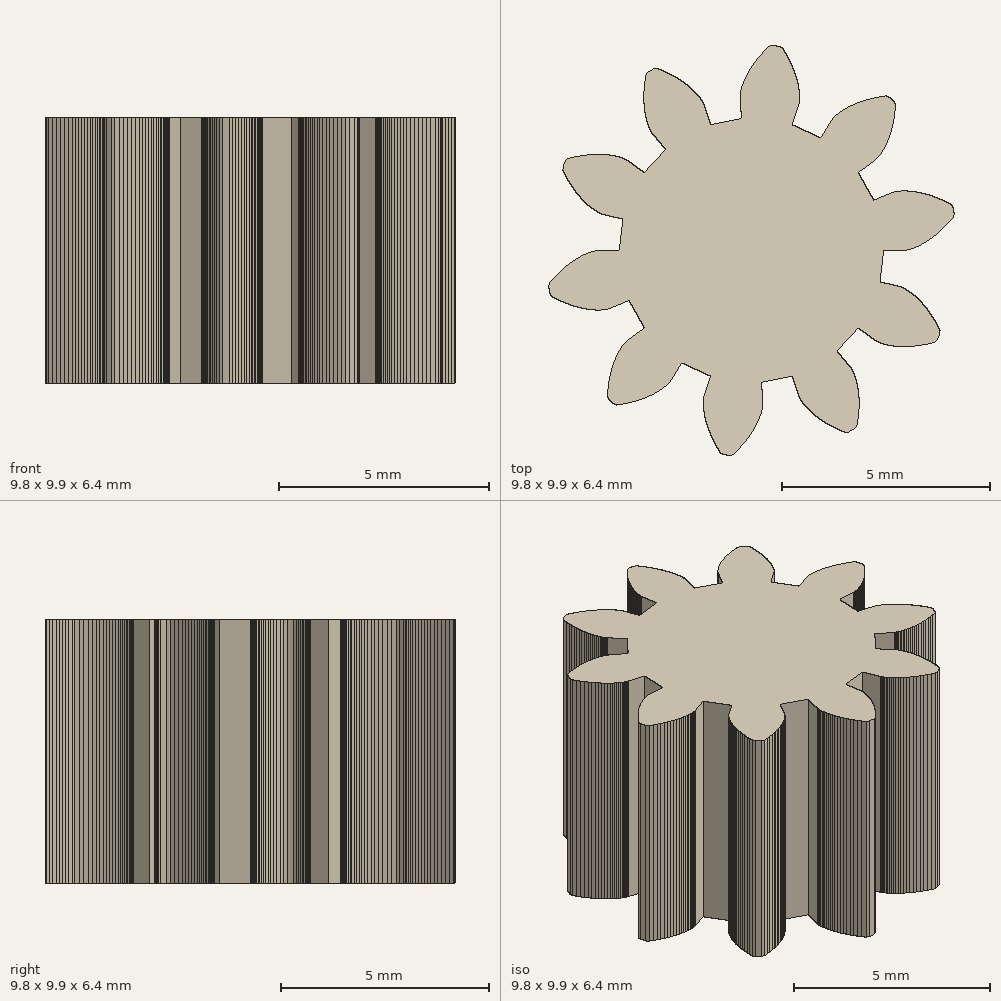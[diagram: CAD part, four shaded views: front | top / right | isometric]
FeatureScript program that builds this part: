
annotation { "Feature Type Name" : "Feature", "Feature Type Description" : "" }
export const myFeature = defineFeature(function(context is Context, id is Id, definition is map)
    precondition{}
    {
        {
            var Q0;
            Q0=qCreatedBy(makeId("Top.planeOp"),FACE);
            var sketch = newSketch(context, id + "F0", { "sketchPlane" : qUnion([Q0])});
            skLineSegment(sketch, "E0", {"start": v(1, 0) * mm, "end": v(1.16, 0) * mm});
            skLineSegment(sketch, "E1", {"start": v(1.16, 0) * mm, "end": v(1.16, 0) * mm});
            skLineSegment(sketch, "E2", {"start": v(1.16, 0) * mm, "end": v(1.17, 0) * mm});
            skLineSegment(sketch, "E3", {"start": v(1.17, 0) * mm, "end": v(1.17, 0) * mm});
            skLineSegment(sketch, "E4", {"start": v(1.17, 0) * mm, "end": v(1.18, 0) * mm});
            skLineSegment(sketch, "E5", {"start": v(1.18, 0) * mm, "end": v(1.19, 0) * mm});
            skLineSegment(sketch, "E6", {"start": v(1.19, 0) * mm, "end": v(1.2, 0) * mm});
            skLineSegment(sketch, "E7", {"start": v(1.2, 0) * mm, "end": v(1.21, 0.01) * mm});
            skLineSegment(sketch, "E8", {"start": v(1.21, 0.01) * mm, "end": v(1.22, 0.01) * mm});
            skLineSegment(sketch, "E9", {"start": v(1.22, 0.01) * mm, "end": v(1.24, 0.02) * mm});
            skLineSegment(sketch, "E10", {"start": v(1.24, 0.02) * mm, "end": v(1.25, 0.02) * mm});
            skLineSegment(sketch, "E11", {"start": v(1.25, 0.02) * mm, "end": v(1.27, 0.03) * mm});
            skLineSegment(sketch, "E12", {"start": v(1.27, 0.03) * mm, "end": v(1.28, 0.04) * mm});
            skLineSegment(sketch, "E13", {"start": v(1.28, 0.04) * mm, "end": v(1.3, 0.05) * mm});
            skLineSegment(sketch, "E14", {"start": v(1.3, 0.05) * mm, "end": v(1.32, 0.06) * mm});
            skLineSegment(sketch, "E15", {"start": v(1.32, 0.06) * mm, "end": v(1.34, 0.07) * mm});
            skLineSegment(sketch, "E16", {"start": v(1.34, 0.07) * mm, "end": v(1.36, 0.08) * mm});
            skLineSegment(sketch, "E17", {"start": v(1.36, 0.08) * mm, "end": v(1.38, 0.1) * mm});
            skLineSegment(sketch, "E18", {"start": v(1.38, 0.1) * mm, "end": v(1.4, 0.12) * mm});
            skLineSegment(sketch, "E19", {"start": v(1.4, 0.12) * mm, "end": v(1.42, 0.13) * mm});
            skLineSegment(sketch, "E20", {"start": v(1.42, 0.13) * mm, "end": v(1.44, 0.15) * mm});
            skLineSegment(sketch, "E21", {"start": v(1.44, 0.15) * mm, "end": v(1.46, 0.18) * mm});
            skLineSegment(sketch, "E22", {"start": v(1.46, 0.18) * mm, "end": v(1.49, 0.2) * mm});
            skLineSegment(sketch, "E23", {"start": v(1.49, 0.2) * mm, "end": v(1.5, 0.22) * mm});
            skLineSegment(sketch, "E24", {"start": v(1.5, 0.22) * mm, "end": v(1.53, 0.25) * mm});
            skLineSegment(sketch, "E25", {"start": v(1.53, 0.25) * mm, "end": v(1.54, 0.28) * mm});
            skLineSegment(sketch, "E26", {"start": v(1.54, 0.28) * mm, "end": v(1.53, 0.33) * mm});
            skLineSegment(sketch, "E27", {"start": v(1.53, 0.33) * mm, "end": v(1.51, 0.35) * mm});
            skLineSegment(sketch, "E28", {"start": v(1.51, 0.35) * mm, "end": v(1.48, 0.37) * mm});
            skLineSegment(sketch, "E29", {"start": v(1.48, 0.37) * mm, "end": v(1.45, 0.38) * mm});
            skLineSegment(sketch, "E30", {"start": v(1.45, 0.38) * mm, "end": v(1.42, 0.4) * mm});
            skLineSegment(sketch, "E31", {"start": v(1.42, 0.4) * mm, "end": v(1.4, 0.4) * mm});
            skLineSegment(sketch, "E32", {"start": v(1.4, 0.4) * mm, "end": v(1.37, 0.41) * mm});
            skLineSegment(sketch, "E33", {"start": v(1.37, 0.41) * mm, "end": v(1.34, 0.42) * mm});
            skLineSegment(sketch, "E34", {"start": v(1.34, 0.42) * mm, "end": v(1.31, 0.43) * mm});
            skLineSegment(sketch, "E35", {"start": v(1.31, 0.43) * mm, "end": v(1.29, 0.44) * mm});
            skLineSegment(sketch, "E36", {"start": v(1.29, 0.44) * mm, "end": v(1.26, 0.44) * mm});
            skLineSegment(sketch, "E37", {"start": v(1.26, 0.44) * mm, "end": v(1.24, 0.45) * mm});
            skLineSegment(sketch, "E38", {"start": v(1.24, 0.45) * mm, "end": v(1.22, 0.45) * mm});
            skLineSegment(sketch, "E39", {"start": v(1.22, 0.45) * mm, "end": v(1.2, 0.45) * mm});
            skLineSegment(sketch, "E40", {"start": v(1.2, 0.45) * mm, "end": v(1.18, 0.45) * mm});
            skLineSegment(sketch, "E41", {"start": v(1.18, 0.45) * mm, "end": v(1.17, 0.45) * mm});
            skLineSegment(sketch, "E42", {"start": v(1.17, 0.45) * mm, "end": v(1.15, 0.45) * mm});
            skLineSegment(sketch, "E43", {"start": v(1.15, 0.45) * mm, "end": v(1.14, 0.45) * mm});
            skLineSegment(sketch, "E44", {"start": v(1.14, 0.45) * mm, "end": v(1.12, 0.45) * mm});
            skLineSegment(sketch, "E45", {"start": v(1.12, 0.45) * mm, "end": v(1.11, 0.45) * mm});
            skLineSegment(sketch, "E46", {"start": v(1.11, 0.45) * mm, "end": v(1.1, 0.45) * mm});
            skLineSegment(sketch, "E47", {"start": v(1.1, 0.45) * mm, "end": v(1.1, 0.45) * mm});
            skLineSegment(sketch, "E48", {"start": v(1.1, 0.45) * mm, "end": v(1.09, 0.44) * mm});
            skLineSegment(sketch, "E49", {"start": v(1.09, 0.44) * mm, "end": v(1.08, 0.44) * mm});
            skLineSegment(sketch, "E50", {"start": v(1.08, 0.44) * mm, "end": v(1.08, 0.44) * mm});
            skLineSegment(sketch, "E51", {"start": v(1.08, 0.44) * mm, "end": v(1.07, 0.44) * mm});
            skLineSegment(sketch, "E52", {"start": v(1.07, 0.44) * mm, "end": v(1.07, 0.44) * mm});
            skLineSegment(sketch, "E53", {"start": v(1.07, 0.44) * mm, "end": v(0.93, 0.38) * mm});
            skLineSegment(sketch, "E54", {"start": v(0.93, 0.38) * mm, "end": v(0.81, 0.59) * mm});
            skLineSegment(sketch, "E55", {"start": v(0.81, 0.59) * mm, "end": v(0.94, 0.68) * mm});
            skLineSegment(sketch, "E56", {"start": v(0.94, 0.68) * mm, "end": v(0.94, 0.68) * mm});
            skLineSegment(sketch, "E57", {"start": v(0.94, 0.68) * mm, "end": v(0.95, 0.69) * mm});
            skLineSegment(sketch, "E58", {"start": v(0.95, 0.69) * mm, "end": v(0.95, 0.7) * mm});
            skLineSegment(sketch, "E59", {"start": v(0.95, 0.7) * mm, "end": v(0.95, 0.7) * mm});
            skLineSegment(sketch, "E60", {"start": v(0.95, 0.7) * mm, "end": v(0.96, 0.7) * mm});
            skLineSegment(sketch, "E61", {"start": v(0.96, 0.7) * mm, "end": v(0.97, 0.71) * mm});
            skLineSegment(sketch, "E62", {"start": v(0.97, 0.71) * mm, "end": v(0.97, 0.72) * mm});
            skLineSegment(sketch, "E63", {"start": v(0.97, 0.72) * mm, "end": v(0.98, 0.73) * mm});
            skLineSegment(sketch, "E64", {"start": v(0.98, 0.73) * mm, "end": v(0.99, 0.74) * mm});
            skLineSegment(sketch, "E65", {"start": v(0.99, 0.74) * mm, "end": v(1, 0.75) * mm});
            skLineSegment(sketch, "E66", {"start": v(1, 0.75) * mm, "end": v(1, 0.77) * mm});
            skLineSegment(sketch, "E67", {"start": v(1, 0.77) * mm, "end": v(1.01, 0.79) * mm});
            skLineSegment(sketch, "E68", {"start": v(1.01, 0.79) * mm, "end": v(1.02, 0.8) * mm});
            skLineSegment(sketch, "E69", {"start": v(1.02, 0.8) * mm, "end": v(1.03, 0.82) * mm});
            skLineSegment(sketch, "E70", {"start": v(1.03, 0.82) * mm, "end": v(1.04, 0.84) * mm});
            skLineSegment(sketch, "E71", {"start": v(1.04, 0.84) * mm, "end": v(1.05, 0.87) * mm});
            skLineSegment(sketch, "E72", {"start": v(1.05, 0.87) * mm, "end": v(1.06, 0.9) * mm});
            skLineSegment(sketch, "E73", {"start": v(1.06, 0.9) * mm, "end": v(1.06, 0.92) * mm});
            skLineSegment(sketch, "E74", {"start": v(1.06, 0.92) * mm, "end": v(1.07, 0.94) * mm});
            skLineSegment(sketch, "E75", {"start": v(1.07, 0.94) * mm, "end": v(1.08, 0.97) * mm});
            skLineSegment(sketch, "E76", {"start": v(1.08, 0.97) * mm, "end": v(1.08, 1) * mm});
            skLineSegment(sketch, "E77", {"start": v(1.08, 1) * mm, "end": v(1.09, 1.04) * mm});
            skLineSegment(sketch, "E78", {"start": v(1.09, 1.04) * mm, "end": v(1.09, 1.07) * mm});
            skLineSegment(sketch, "E79", {"start": v(1.09, 1.07) * mm, "end": v(1.1, 1.1) * mm});
            skLineSegment(sketch, "E80", {"start": v(1.1, 1.1) * mm, "end": v(1.08, 1.13) * mm});
            skLineSegment(sketch, "E81", {"start": v(1.08, 1.13) * mm, "end": v(1.04, 1.16) * mm});
            skLineSegment(sketch, "E82", {"start": v(1.04, 1.16) * mm, "end": v(1.02, 1.17) * mm});
            skLineSegment(sketch, "E83", {"start": v(1.02, 1.17) * mm, "end": v(0.98, 1.17) * mm});
            skLineSegment(sketch, "E84", {"start": v(0.98, 1.17) * mm, "end": v(0.95, 1.16) * mm});
            skLineSegment(sketch, "E85", {"start": v(0.95, 1.16) * mm, "end": v(0.92, 1.15) * mm});
            skLineSegment(sketch, "E86", {"start": v(0.92, 1.15) * mm, "end": v(0.89, 1.15) * mm});
            skLineSegment(sketch, "E87", {"start": v(0.89, 1.15) * mm, "end": v(0.86, 1.14) * mm});
            skLineSegment(sketch, "E88", {"start": v(0.86, 1.14) * mm, "end": v(0.83, 1.13) * mm});
            skLineSegment(sketch, "E89", {"start": v(0.83, 1.13) * mm, "end": v(0.8, 1.12) * mm});
            skLineSegment(sketch, "E90", {"start": v(0.8, 1.12) * mm, "end": v(0.79, 1.1) * mm});
            skLineSegment(sketch, "E91", {"start": v(0.79, 1.1) * mm, "end": v(0.76, 1.1) * mm});
            skLineSegment(sketch, "E92", {"start": v(0.76, 1.1) * mm, "end": v(0.74, 1.1) * mm});
            skLineSegment(sketch, "E93", {"start": v(0.74, 1.1) * mm, "end": v(0.72, 1.08) * mm});
            skLineSegment(sketch, "E94", {"start": v(0.72, 1.08) * mm, "end": v(0.7, 1.07) * mm});
            skLineSegment(sketch, "E95", {"start": v(0.7, 1.07) * mm, "end": v(0.7, 1.06) * mm});
            skLineSegment(sketch, "E96", {"start": v(0.7, 1.06) * mm, "end": v(0.68, 1.05) * mm});
            skLineSegment(sketch, "E97", {"start": v(0.68, 1.05) * mm, "end": v(0.67, 1.04) * mm});
            skLineSegment(sketch, "E98", {"start": v(0.67, 1.04) * mm, "end": v(0.65, 1.03) * mm});
            skLineSegment(sketch, "E99", {"start": v(0.65, 1.03) * mm, "end": v(0.64, 1.02) * mm});
            skLineSegment(sketch, "E100", {"start": v(0.64, 1.02) * mm, "end": v(0.64, 1.02) * mm});
            skLineSegment(sketch, "E101", {"start": v(0.64, 1.02) * mm, "end": v(0.63, 1) * mm});
            skLineSegment(sketch, "E102", {"start": v(0.63, 1) * mm, "end": v(0.62, 1) * mm});
            skLineSegment(sketch, "E103", {"start": v(0.62, 1) * mm, "end": v(0.62, 1) * mm});
            skLineSegment(sketch, "E104", {"start": v(0.62, 1) * mm, "end": v(0.61, 1) * mm});
            skLineSegment(sketch, "E105", {"start": v(0.61, 1) * mm, "end": v(0.61, 1) * mm});
            skLineSegment(sketch, "E106", {"start": v(0.61, 1) * mm, "end": v(0.61, 0.99) * mm});
            skLineSegment(sketch, "E107", {"start": v(0.61, 0.99) * mm, "end": v(0.6, 0.99) * mm});
            skLineSegment(sketch, "E108", {"start": v(0.6, 0.99) * mm, "end": v(0.53, 0.85) * mm});
            skLineSegment(sketch, "E109", {"start": v(0.53, 0.85) * mm, "end": v(0.3, 0.95) * mm});
            skLineSegment(sketch, "E110", {"start": v(0.3, 0.95) * mm, "end": v(0.36, 1.1) * mm});
            skLineSegment(sketch, "E111", {"start": v(0.36, 1.1) * mm, "end": v(0.36, 1.1) * mm});
            skLineSegment(sketch, "E112", {"start": v(0.36, 1.1) * mm, "end": v(0.36, 1.11) * mm});
            skLineSegment(sketch, "E113", {"start": v(0.36, 1.11) * mm, "end": v(0.36, 1.12) * mm});
            skLineSegment(sketch, "E114", {"start": v(0.36, 1.12) * mm, "end": v(0.36, 1.12) * mm});
            skLineSegment(sketch, "E115", {"start": v(0.36, 1.12) * mm, "end": v(0.36, 1.13) * mm});
            skLineSegment(sketch, "E116", {"start": v(0.36, 1.13) * mm, "end": v(0.36, 1.14) * mm});
            skLineSegment(sketch, "E117", {"start": v(0.36, 1.14) * mm, "end": v(0.36, 1.15) * mm});
            skLineSegment(sketch, "E118", {"start": v(0.36, 1.15) * mm, "end": v(0.36, 1.17) * mm});
            skLineSegment(sketch, "E119", {"start": v(0.36, 1.17) * mm, "end": v(0.36, 1.18) * mm});
            skLineSegment(sketch, "E120", {"start": v(0.36, 1.18) * mm, "end": v(0.36, 1.2) * mm});
            skLineSegment(sketch, "E121", {"start": v(0.36, 1.2) * mm, "end": v(0.36, 1.21) * mm});
            skLineSegment(sketch, "E122", {"start": v(0.36, 1.21) * mm, "end": v(0.36, 1.23) * mm});
            skLineSegment(sketch, "E123", {"start": v(0.36, 1.23) * mm, "end": v(0.36, 1.25) * mm});
            skLineSegment(sketch, "E124", {"start": v(0.36, 1.25) * mm, "end": v(0.35, 1.27) * mm});
            skLineSegment(sketch, "E125", {"start": v(0.35, 1.27) * mm, "end": v(0.35, 1.3) * mm});
            skLineSegment(sketch, "E126", {"start": v(0.35, 1.3) * mm, "end": v(0.34, 1.32) * mm});
            skLineSegment(sketch, "E127", {"start": v(0.34, 1.32) * mm, "end": v(0.33, 1.34) * mm});
            skLineSegment(sketch, "E128", {"start": v(0.33, 1.34) * mm, "end": v(0.32, 1.37) * mm});
            skLineSegment(sketch, "E129", {"start": v(0.32, 1.37) * mm, "end": v(0.31, 1.4) * mm});
            skLineSegment(sketch, "E130", {"start": v(0.31, 1.4) * mm, "end": v(0.3, 1.42) * mm});
            skLineSegment(sketch, "E131", {"start": v(0.3, 1.42) * mm, "end": v(0.29, 1.45) * mm});
            skLineSegment(sketch, "E132", {"start": v(0.29, 1.45) * mm, "end": v(0.27, 1.48) * mm});
            skLineSegment(sketch, "E133", {"start": v(0.27, 1.48) * mm, "end": v(0.25, 1.5) * mm});
            skLineSegment(sketch, "E134", {"start": v(0.25, 1.5) * mm, "end": v(0.23, 1.54) * mm});
            skLineSegment(sketch, "E135", {"start": v(0.23, 1.54) * mm, "end": v(0.21, 1.55) * mm});
            skLineSegment(sketch, "E136", {"start": v(0.21, 1.55) * mm, "end": v(0.16, 1.55) * mm});
            skLineSegment(sketch, "E137", {"start": v(0.16, 1.55) * mm, "end": v(0.14, 1.55) * mm});
            skLineSegment(sketch, "E138", {"start": v(0.14, 1.55) * mm, "end": v(0.11, 1.52) * mm});
            skLineSegment(sketch, "E139", {"start": v(0.11, 1.52) * mm, "end": v(0.09, 1.5) * mm});
            skLineSegment(sketch, "E140", {"start": v(0.09, 1.5) * mm, "end": v(0.07, 1.47) * mm});
            skLineSegment(sketch, "E141", {"start": v(0.07, 1.47) * mm, "end": v(0.05, 1.45) * mm});
            skLineSegment(sketch, "E142", {"start": v(0.05, 1.45) * mm, "end": v(0.03, 1.43) * mm});
            skLineSegment(sketch, "E143", {"start": v(0.03, 1.43) * mm, "end": v(0.01, 1.4) * mm});
            skLineSegment(sketch, "E144", {"start": v(0.01, 1.4) * mm, "end": v(0, 1.38) * mm});
            skLineSegment(sketch, "E145", {"start": v(0, 1.38) * mm, "end": v(-0.02, 1.36) * mm});
            skLineSegment(sketch, "E146", {"start": v(-0.02, 1.36) * mm, "end": v(-0.03, 1.34) * mm});
            skLineSegment(sketch, "E147", {"start": v(-0.03, 1.34) * mm, "end": v(-0.04, 1.32) * mm});
            skLineSegment(sketch, "E148", {"start": v(-0.04, 1.32) * mm, "end": v(-0.05, 1.3) * mm});
            skLineSegment(sketch, "E149", {"start": v(-0.05, 1.3) * mm, "end": v(-0.06, 1.28) * mm});
            skLineSegment(sketch, "E150", {"start": v(-0.06, 1.28) * mm, "end": v(-0.06, 1.26) * mm});
            skLineSegment(sketch, "E151", {"start": v(-0.06, 1.26) * mm, "end": v(-0.07, 1.25) * mm});
            skLineSegment(sketch, "E152", {"start": v(-0.07, 1.25) * mm, "end": v(-0.07, 1.23) * mm});
            skLineSegment(sketch, "E153", {"start": v(-0.07, 1.23) * mm, "end": v(-0.08, 1.22) * mm});
            skLineSegment(sketch, "E154", {"start": v(-0.08, 1.22) * mm, "end": v(-0.08, 1.2) * mm});
            skLineSegment(sketch, "E155", {"start": v(-0.08, 1.2) * mm, "end": v(-0.08, 1.2) * mm});
            skLineSegment(sketch, "E156", {"start": v(-0.08, 1.2) * mm, "end": v(-0.08, 1.19) * mm});
            skLineSegment(sketch, "E157", {"start": v(-0.08, 1.19) * mm, "end": v(-0.09, 1.18) * mm});
            skLineSegment(sketch, "E158", {"start": v(-0.09, 1.18) * mm, "end": v(-0.09, 1.17) * mm});
            skLineSegment(sketch, "E159", {"start": v(-0.09, 1.17) * mm, "end": v(-0.09, 1.17) * mm});
            skLineSegment(sketch, "E160", {"start": v(-0.09, 1.17) * mm, "end": v(-0.09, 1.16) * mm});
            skLineSegment(sketch, "E161", {"start": v(-0.09, 1.16) * mm, "end": v(-0.09, 1.16) * mm});
            skLineSegment(sketch, "E162", {"start": v(-0.09, 1.16) * mm, "end": v(-0.08, 1) * mm});
            skLineSegment(sketch, "E163", {"start": v(-0.08, 1) * mm, "end": v(-0.3, 0.95) * mm});
            skLineSegment(sketch, "E164", {"start": v(-0.3, 0.95) * mm, "end": v(-0.36, 1.1) * mm});
            skLineSegment(sketch, "E165", {"start": v(-0.36, 1.1) * mm, "end": v(-0.36, 1.1) * mm});
            skLineSegment(sketch, "E166", {"start": v(-0.36, 1.1) * mm, "end": v(-0.36, 1.11) * mm});
            skLineSegment(sketch, "E167", {"start": v(-0.36, 1.11) * mm, "end": v(-0.36, 1.12) * mm});
            skLineSegment(sketch, "E168", {"start": v(-0.36, 1.12) * mm, "end": v(-0.37, 1.12) * mm});
            skLineSegment(sketch, "E169", {"start": v(-0.37, 1.12) * mm, "end": v(-0.37, 1.13) * mm});
            skLineSegment(sketch, "E170", {"start": v(-0.37, 1.13) * mm, "end": v(-0.38, 1.14) * mm});
            skLineSegment(sketch, "E171", {"start": v(-0.38, 1.14) * mm, "end": v(-0.38, 1.15) * mm});
            skLineSegment(sketch, "E172", {"start": v(-0.38, 1.15) * mm, "end": v(-0.4, 1.16) * mm});
            skLineSegment(sketch, "E173", {"start": v(-0.4, 1.16) * mm, "end": v(-0.4, 1.17) * mm});
            skLineSegment(sketch, "E174", {"start": v(-0.4, 1.17) * mm, "end": v(-0.4, 1.18) * mm});
            skLineSegment(sketch, "E175", {"start": v(-0.4, 1.18) * mm, "end": v(-0.42, 1.2) * mm});
            skLineSegment(sketch, "E176", {"start": v(-0.42, 1.2) * mm, "end": v(-0.43, 1.2) * mm});
            skLineSegment(sketch, "E177", {"start": v(-0.43, 1.2) * mm, "end": v(-0.45, 1.22) * mm});
            skLineSegment(sketch, "E178", {"start": v(-0.45, 1.22) * mm, "end": v(-0.46, 1.23) * mm});
            skLineSegment(sketch, "E179", {"start": v(-0.46, 1.23) * mm, "end": v(-0.48, 1.25) * mm});
            skLineSegment(sketch, "E180", {"start": v(-0.48, 1.25) * mm, "end": v(-0.5, 1.26) * mm});
            skLineSegment(sketch, "E181", {"start": v(-0.5, 1.26) * mm, "end": v(-0.52, 1.28) * mm});
            skLineSegment(sketch, "E182", {"start": v(-0.52, 1.28) * mm, "end": v(-0.54, 1.3) * mm});
            skLineSegment(sketch, "E183", {"start": v(-0.54, 1.3) * mm, "end": v(-0.57, 1.3) * mm});
            skLineSegment(sketch, "E184", {"start": v(-0.57, 1.3) * mm, "end": v(-0.6, 1.32) * mm});
            skLineSegment(sketch, "E185", {"start": v(-0.6, 1.32) * mm, "end": v(-0.62, 1.34) * mm});
            skLineSegment(sketch, "E186", {"start": v(-0.62, 1.34) * mm, "end": v(-0.65, 1.35) * mm});
            skLineSegment(sketch, "E187", {"start": v(-0.65, 1.35) * mm, "end": v(-0.68, 1.37) * mm});
            skLineSegment(sketch, "E188", {"start": v(-0.68, 1.37) * mm, "end": v(-0.71, 1.38) * mm});
            skLineSegment(sketch, "E189", {"start": v(-0.71, 1.38) * mm, "end": v(-0.74, 1.38) * mm});
            skLineSegment(sketch, "E190", {"start": v(-0.74, 1.38) * mm, "end": v(-0.79, 1.36) * mm});
            skLineSegment(sketch, "E191", {"start": v(-0.78, 1.35) * mm, "end": v(-0.8, 1.33) * mm});
            skLineSegment(sketch, "E192", {"start": v(-0.8, 1.33) * mm, "end": v(-0.8, 1.3) * mm});
            skLineSegment(sketch, "E193", {"start": v(-0.8, 1.3) * mm, "end": v(-0.81, 1.26) * mm});
            skLineSegment(sketch, "E194", {"start": v(-0.81, 1.26) * mm, "end": v(-0.81, 1.23) * mm});
            skLineSegment(sketch, "E195", {"start": v(-0.81, 1.23) * mm, "end": v(-0.82, 1.2) * mm});
            skLineSegment(sketch, "E196", {"start": v(-0.82, 1.2) * mm, "end": v(-0.82, 1.17) * mm});
            skLineSegment(sketch, "E197", {"start": v(-0.82, 1.17) * mm, "end": v(-0.82, 1.14) * mm});
            skLineSegment(sketch, "E198", {"start": v(-0.82, 1.14) * mm, "end": v(-0.81, 1.12) * mm});
            skLineSegment(sketch, "E199", {"start": v(-0.81, 1.12) * mm, "end": v(-0.81, 1.09) * mm});
            skLineSegment(sketch, "E200", {"start": v(-0.81, 1.09) * mm, "end": v(-0.81, 1.07) * mm});
            skLineSegment(sketch, "E201", {"start": v(-0.81, 1.07) * mm, "end": v(-0.8, 1.04) * mm});
            skLineSegment(sketch, "E202", {"start": v(-0.8, 1.04) * mm, "end": v(-0.8, 1.02) * mm});
            skLineSegment(sketch, "E203", {"start": v(-0.8, 1.02) * mm, "end": v(-0.8, 1) * mm});
            skLineSegment(sketch, "E204", {"start": v(-0.8, 1) * mm, "end": v(-0.8, 0.99) * mm});
            skLineSegment(sketch, "E205", {"start": v(-0.8, 0.99) * mm, "end": v(-0.79, 0.97) * mm});
            skLineSegment(sketch, "E206", {"start": v(-0.79, 0.97) * mm, "end": v(-0.78, 0.95) * mm});
            skLineSegment(sketch, "E207", {"start": v(-0.78, 0.95) * mm, "end": v(-0.78, 0.94) * mm});
            skLineSegment(sketch, "E208", {"start": v(-0.78, 0.94) * mm, "end": v(-0.78, 0.93) * mm});
            skLineSegment(sketch, "E209", {"start": v(-0.78, 0.93) * mm, "end": v(-0.77, 0.92) * mm});
            skLineSegment(sketch, "E210", {"start": v(-0.77, 0.92) * mm, "end": v(-0.77, 0.91) * mm});
            skLineSegment(sketch, "E211", {"start": v(-0.77, 0.91) * mm, "end": v(-0.76, 0.9) * mm});
            skLineSegment(sketch, "E212", {"start": v(-0.76, 0.9) * mm, "end": v(-0.76, 0.9) * mm});
            skLineSegment(sketch, "E213", {"start": v(-0.76, 0.9) * mm, "end": v(-0.75, 0.89) * mm});
            skLineSegment(sketch, "E214", {"start": v(-0.75, 0.89) * mm, "end": v(-0.75, 0.89) * mm});
            skLineSegment(sketch, "E215", {"start": v(-0.75, 0.89) * mm, "end": v(-0.75, 0.88) * mm});
            skLineSegment(sketch, "E216", {"start": v(-0.75, 0.88) * mm, "end": v(-0.65, 0.76) * mm});
            skLineSegment(sketch, "E217", {"start": v(-0.65, 0.76) * mm, "end": v(-0.81, 0.59) * mm});
            skLineSegment(sketch, "E218", {"start": v(-0.81, 0.59) * mm, "end": v(-0.94, 0.68) * mm});
            skLineSegment(sketch, "E219", {"start": v(-0.94, 0.68) * mm, "end": v(-0.94, 0.68) * mm});
            skLineSegment(sketch, "E220", {"start": v(-0.94, 0.68) * mm, "end": v(-0.95, 0.69) * mm});
            skLineSegment(sketch, "E221", {"start": v(-0.95, 0.69) * mm, "end": v(-0.95, 0.69) * mm});
            skLineSegment(sketch, "E222", {"start": v(-0.95, 0.69) * mm, "end": v(-0.96, 0.7) * mm});
            skLineSegment(sketch, "E223", {"start": v(-0.96, 0.7) * mm, "end": v(-0.97, 0.7) * mm});
            skLineSegment(sketch, "E224", {"start": v(-0.97, 0.7) * mm, "end": v(-0.97, 0.7) * mm});
            skLineSegment(sketch, "E225", {"start": v(-0.97, 0.7) * mm, "end": v(-0.98, 0.7) * mm});
            skLineSegment(sketch, "E226", {"start": v(-0.98, 0.7) * mm, "end": v(-1, 0.7) * mm});
            skLineSegment(sketch, "E227", {"start": v(-1, 0.7) * mm, "end": v(-1.01, 0.71) * mm});
            skLineSegment(sketch, "E228", {"start": v(-1.01, 0.71) * mm, "end": v(-1.03, 0.71) * mm});
            skLineSegment(sketch, "E229", {"start": v(-1.03, 0.71) * mm, "end": v(-1.04, 0.72) * mm});
            skLineSegment(sketch, "E230", {"start": v(-1.04, 0.72) * mm, "end": v(-1.06, 0.72) * mm});
            skLineSegment(sketch, "E231", {"start": v(-1.06, 0.72) * mm, "end": v(-1.08, 0.72) * mm});
            skLineSegment(sketch, "E232", {"start": v(-1.08, 0.72) * mm, "end": v(-1.1, 0.73) * mm});
            skLineSegment(sketch, "E233", {"start": v(-1.1, 0.73) * mm, "end": v(-1.12, 0.73) * mm});
            skLineSegment(sketch, "E234", {"start": v(-1.12, 0.73) * mm, "end": v(-1.15, 0.73) * mm});
            skLineSegment(sketch, "E235", {"start": v(-1.15, 0.73) * mm, "end": v(-1.17, 0.73) * mm});
            skLineSegment(sketch, "E236", {"start": v(-1.17, 0.73) * mm, "end": v(-1.2, 0.73) * mm});
            skLineSegment(sketch, "E237", {"start": v(-1.2, 0.73) * mm, "end": v(-1.23, 0.73) * mm});
            skLineSegment(sketch, "E238", {"start": v(-1.23, 0.73) * mm, "end": v(-1.26, 0.72) * mm});
            skLineSegment(sketch, "E239", {"start": v(-1.26, 0.72) * mm, "end": v(-1.29, 0.72) * mm});
            skLineSegment(sketch, "E240", {"start": v(-1.29, 0.72) * mm, "end": v(-1.32, 0.71) * mm});
            skLineSegment(sketch, "E241", {"start": v(-1.32, 0.71) * mm, "end": v(-1.35, 0.7) * mm});
            skLineSegment(sketch, "E242", {"start": v(-1.35, 0.7) * mm, "end": v(-1.39, 0.7) * mm});
            skLineSegment(sketch, "E243", {"start": v(-1.39, 0.7) * mm, "end": v(-1.4, 0.68) * mm});
            skLineSegment(sketch, "E244", {"start": v(-1.4, 0.68) * mm, "end": v(-1.43, 0.63) * mm});
            skLineSegment(sketch, "E245", {"start": v(-1.43, 0.63) * mm, "end": v(-1.43, 0.6) * mm});
            skLineSegment(sketch, "E246", {"start": v(-1.43, 0.6) * mm, "end": v(-1.41, 0.58) * mm});
            skLineSegment(sketch, "E247", {"start": v(-1.41, 0.58) * mm, "end": v(-1.4, 0.55) * mm});
            skLineSegment(sketch, "E248", {"start": v(-1.4, 0.55) * mm, "end": v(-1.38, 0.52) * mm});
            skLineSegment(sketch, "E249", {"start": v(-1.38, 0.52) * mm, "end": v(-1.36, 0.5) * mm});
            skLineSegment(sketch, "E250", {"start": v(-1.36, 0.5) * mm, "end": v(-1.35, 0.47) * mm});
            skLineSegment(sketch, "E251", {"start": v(-1.35, 0.47) * mm, "end": v(-1.33, 0.44) * mm});
            skLineSegment(sketch, "E252", {"start": v(-1.33, 0.44) * mm, "end": v(-1.31, 0.42) * mm});
            skLineSegment(sketch, "E253", {"start": v(-1.31, 0.42) * mm, "end": v(-1.3, 0.4) * mm});
            skLineSegment(sketch, "E254", {"start": v(-1.3, 0.4) * mm, "end": v(-1.28, 0.39) * mm});
            skLineSegment(sketch, "E255", {"start": v(-1.28, 0.39) * mm, "end": v(-1.27, 0.37) * mm});
            skLineSegment(sketch, "E256", {"start": v(-1.27, 0.37) * mm, "end": v(-1.25, 0.36) * mm});
            skLineSegment(sketch, "E257", {"start": v(-1.25, 0.36) * mm, "end": v(-1.24, 0.34) * mm});
            skLineSegment(sketch, "E258", {"start": v(-1.24, 0.34) * mm, "end": v(-1.22, 0.33) * mm});
            skLineSegment(sketch, "E259", {"start": v(-1.22, 0.33) * mm, "end": v(-1.2, 0.32) * mm});
            skLineSegment(sketch, "E260", {"start": v(-1.2, 0.32) * mm, "end": v(-1.2, 0.31) * mm});
            skLineSegment(sketch, "E261", {"start": v(-1.2, 0.31) * mm, "end": v(-1.18, 0.3) * mm});
            skLineSegment(sketch, "E262", {"start": v(-1.18, 0.3) * mm, "end": v(-1.17, 0.3) * mm});
            skLineSegment(sketch, "E263", {"start": v(-1.17, 0.3) * mm, "end": v(-1.16, 0.3) * mm});
            skLineSegment(sketch, "E264", {"start": v(-1.16, 0.3) * mm, "end": v(-1.15, 0.29) * mm});
            skLineSegment(sketch, "E265", {"start": v(-1.15, 0.29) * mm, "end": v(-1.15, 0.28) * mm});
            skLineSegment(sketch, "E266", {"start": v(-1.15, 0.28) * mm, "end": v(-1.14, 0.28) * mm});
            skLineSegment(sketch, "E267", {"start": v(-1.14, 0.28) * mm, "end": v(-1.14, 0.28) * mm});
            skLineSegment(sketch, "E268", {"start": v(-1.14, 0.28) * mm, "end": v(-1.13, 0.28) * mm});
            skLineSegment(sketch, "E269", {"start": v(-1.13, 0.28) * mm, "end": v(-1.13, 0.28) * mm});
            skLineSegment(sketch, "E270", {"start": v(-1.13, 0.28) * mm, "end": v(-1.13, 0.27) * mm});
            skLineSegment(sketch, "E271", {"start": v(-1.13, 0.27) * mm, "end": v(-0.97, 0.24) * mm});
            skLineSegment(sketch, "E272", {"start": v(-0.97, 0.24) * mm, "end": v(-1, 0) * mm});
            skLineSegment(sketch, "E273", {"start": v(-1, 0) * mm, "end": v(-1.16, 0) * mm});
            skLineSegment(sketch, "E274", {"start": v(-1.16, 0) * mm, "end": v(-1.16, 0) * mm});
            skLineSegment(sketch, "E275", {"start": v(-1.16, 0) * mm, "end": v(-1.17, 0) * mm});
            skLineSegment(sketch, "E276", {"start": v(-1.17, 0) * mm, "end": v(-1.17, 0) * mm});
            skLineSegment(sketch, "E277", {"start": v(-1.17, 0) * mm, "end": v(-1.18, 0) * mm});
            skLineSegment(sketch, "E278", {"start": v(-1.18, 0) * mm, "end": v(-1.19, 0) * mm});
            skLineSegment(sketch, "E279", {"start": v(-1.19, 0) * mm, "end": v(-1.2, 0) * mm});
            skLineSegment(sketch, "E280", {"start": v(-1.2, 0) * mm, "end": v(-1.21, -0.01) * mm});
            skLineSegment(sketch, "E281", {"start": v(-1.21, -0.01) * mm, "end": v(-1.22, -0.01) * mm});
            skLineSegment(sketch, "E282", {"start": v(-1.22, -0.01) * mm, "end": v(-1.24, -0.02) * mm});
            skLineSegment(sketch, "E283", {"start": v(-1.24, -0.02) * mm, "end": v(-1.25, -0.02) * mm});
            skLineSegment(sketch, "E284", {"start": v(-1.25, -0.02) * mm, "end": v(-1.27, -0.03) * mm});
            skLineSegment(sketch, "E285", {"start": v(-1.27, -0.03) * mm, "end": v(-1.28, -0.04) * mm});
            skLineSegment(sketch, "E286", {"start": v(-1.28, -0.04) * mm, "end": v(-1.3, -0.05) * mm});
            skLineSegment(sketch, "E287", {"start": v(-1.3, -0.05) * mm, "end": v(-1.32, -0.06) * mm});
            skLineSegment(sketch, "E288", {"start": v(-1.32, -0.06) * mm, "end": v(-1.34, -0.07) * mm});
            skLineSegment(sketch, "E289", {"start": v(-1.34, -0.07) * mm, "end": v(-1.36, -0.08) * mm});
            skLineSegment(sketch, "E290", {"start": v(-1.36, -0.08) * mm, "end": v(-1.38, -0.1) * mm});
            skLineSegment(sketch, "E291", {"start": v(-1.38, -0.1) * mm, "end": v(-1.4, -0.12) * mm});
            skLineSegment(sketch, "E292", {"start": v(-1.4, -0.12) * mm, "end": v(-1.42, -0.13) * mm});
            skLineSegment(sketch, "E293", {"start": v(-1.42, -0.13) * mm, "end": v(-1.44, -0.15) * mm});
            skLineSegment(sketch, "E294", {"start": v(-1.44, -0.15) * mm, "end": v(-1.46, -0.18) * mm});
            skLineSegment(sketch, "E295", {"start": v(-1.46, -0.18) * mm, "end": v(-1.49, -0.2) * mm});
            skLineSegment(sketch, "E296", {"start": v(-1.49, -0.2) * mm, "end": v(-1.5, -0.22) * mm});
            skLineSegment(sketch, "E297", {"start": v(-1.5, -0.22) * mm, "end": v(-1.53, -0.25) * mm});
            skLineSegment(sketch, "E298", {"start": v(-1.53, -0.25) * mm, "end": v(-1.54, -0.28) * mm});
            skLineSegment(sketch, "E299", {"start": v(-1.54, -0.28) * mm, "end": v(-1.53, -0.33) * mm});
            skLineSegment(sketch, "E300", {"start": v(-1.53, -0.33) * mm, "end": v(-1.51, -0.35) * mm});
            skLineSegment(sketch, "E301", {"start": v(-1.51, -0.35) * mm, "end": v(-1.48, -0.37) * mm});
            skLineSegment(sketch, "E302", {"start": v(-1.48, -0.37) * mm, "end": v(-1.45, -0.38) * mm});
            skLineSegment(sketch, "E303", {"start": v(-1.45, -0.38) * mm, "end": v(-1.42, -0.4) * mm});
            skLineSegment(sketch, "E304", {"start": v(-1.42, -0.4) * mm, "end": v(-1.4, -0.4) * mm});
            skLineSegment(sketch, "E305", {"start": v(-1.4, -0.4) * mm, "end": v(-1.37, -0.41) * mm});
            skLineSegment(sketch, "E306", {"start": v(-1.37, -0.41) * mm, "end": v(-1.34, -0.42) * mm});
            skLineSegment(sketch, "E307", {"start": v(-1.34, -0.42) * mm, "end": v(-1.31, -0.43) * mm});
            skLineSegment(sketch, "E308", {"start": v(-1.31, -0.43) * mm, "end": v(-1.29, -0.44) * mm});
            skLineSegment(sketch, "E309", {"start": v(-1.29, -0.44) * mm, "end": v(-1.26, -0.44) * mm});
            skLineSegment(sketch, "E310", {"start": v(-1.26, -0.44) * mm, "end": v(-1.24, -0.45) * mm});
            skLineSegment(sketch, "E311", {"start": v(-1.24, -0.45) * mm, "end": v(-1.22, -0.45) * mm});
            skLineSegment(sketch, "E312", {"start": v(-1.22, -0.45) * mm, "end": v(-1.2, -0.45) * mm});
            skLineSegment(sketch, "E313", {"start": v(-1.2, -0.45) * mm, "end": v(-1.18, -0.45) * mm});
            skLineSegment(sketch, "E314", {"start": v(-1.18, -0.45) * mm, "end": v(-1.17, -0.45) * mm});
            skLineSegment(sketch, "E315", {"start": v(-1.17, -0.45) * mm, "end": v(-1.15, -0.45) * mm});
            skLineSegment(sketch, "E316", {"start": v(-1.15, -0.45) * mm, "end": v(-1.14, -0.45) * mm});
            skLineSegment(sketch, "E317", {"start": v(-1.14, -0.45) * mm, "end": v(-1.12, -0.45) * mm});
            skLineSegment(sketch, "E318", {"start": v(-1.12, -0.45) * mm, "end": v(-1.11, -0.45) * mm});
            skLineSegment(sketch, "E319", {"start": v(-1.11, -0.45) * mm, "end": v(-1.1, -0.45) * mm});
            skLineSegment(sketch, "E320", {"start": v(-1.1, -0.45) * mm, "end": v(-1.1, -0.45) * mm});
            skLineSegment(sketch, "E321", {"start": v(-1.1, -0.45) * mm, "end": v(-1.09, -0.44) * mm});
            skLineSegment(sketch, "E322", {"start": v(-1.09, -0.44) * mm, "end": v(-1.08, -0.44) * mm});
            skLineSegment(sketch, "E323", {"start": v(-1.08, -0.44) * mm, "end": v(-1.08, -0.44) * mm});
            skLineSegment(sketch, "E324", {"start": v(-1.08, -0.44) * mm, "end": v(-1.07, -0.44) * mm});
            skLineSegment(sketch, "E325", {"start": v(-1.07, -0.44) * mm, "end": v(-1.07, -0.44) * mm});
            skLineSegment(sketch, "E326", {"start": v(-1.07, -0.44) * mm, "end": v(-0.93, -0.38) * mm});
            skLineSegment(sketch, "E327", {"start": v(-0.93, -0.38) * mm, "end": v(-0.81, -0.59) * mm});
            skLineSegment(sketch, "E328", {"start": v(-0.81, -0.59) * mm, "end": v(-0.94, -0.68) * mm});
            skLineSegment(sketch, "E329", {"start": v(-0.94, -0.68) * mm, "end": v(-0.94, -0.68) * mm});
            skLineSegment(sketch, "E330", {"start": v(-0.94, -0.68) * mm, "end": v(-0.95, -0.69) * mm});
            skLineSegment(sketch, "E331", {"start": v(-0.95, -0.69) * mm, "end": v(-0.95, -0.7) * mm});
            skLineSegment(sketch, "E332", {"start": v(-0.95, -0.7) * mm, "end": v(-0.95, -0.7) * mm});
            skLineSegment(sketch, "E333", {"start": v(-0.95, -0.7) * mm, "end": v(-0.96, -0.7) * mm});
            skLineSegment(sketch, "E334", {"start": v(-0.96, -0.7) * mm, "end": v(-0.97, -0.71) * mm});
            skLineSegment(sketch, "E335", {"start": v(-0.97, -0.71) * mm, "end": v(-0.97, -0.72) * mm});
            skLineSegment(sketch, "E336", {"start": v(-0.97, -0.72) * mm, "end": v(-0.98, -0.73) * mm});
            skLineSegment(sketch, "E337", {"start": v(-0.98, -0.73) * mm, "end": v(-0.99, -0.74) * mm});
            skLineSegment(sketch, "E338", {"start": v(-0.99, -0.74) * mm, "end": v(-1, -0.75) * mm});
            skLineSegment(sketch, "E339", {"start": v(-1, -0.75) * mm, "end": v(-1, -0.77) * mm});
            skLineSegment(sketch, "E340", {"start": v(-1, -0.77) * mm, "end": v(-1.01, -0.79) * mm});
            skLineSegment(sketch, "E341", {"start": v(-1.01, -0.79) * mm, "end": v(-1.02, -0.8) * mm});
            skLineSegment(sketch, "E342", {"start": v(-1.02, -0.8) * mm, "end": v(-1.03, -0.82) * mm});
            skLineSegment(sketch, "E343", {"start": v(-1.03, -0.82) * mm, "end": v(-1.04, -0.84) * mm});
            skLineSegment(sketch, "E344", {"start": v(-1.04, -0.84) * mm, "end": v(-1.05, -0.87) * mm});
            skLineSegment(sketch, "E345", {"start": v(-1.05, -0.87) * mm, "end": v(-1.06, -0.9) * mm});
            skLineSegment(sketch, "E346", {"start": v(-1.06, -0.9) * mm, "end": v(-1.06, -0.92) * mm});
            skLineSegment(sketch, "E347", {"start": v(-1.06, -0.92) * mm, "end": v(-1.07, -0.94) * mm});
            skLineSegment(sketch, "E348", {"start": v(-1.07, -0.94) * mm, "end": v(-1.08, -0.97) * mm});
            skLineSegment(sketch, "E349", {"start": v(-1.08, -0.97) * mm, "end": v(-1.08, -1) * mm});
            skLineSegment(sketch, "E350", {"start": v(-1.08, -1) * mm, "end": v(-1.09, -1.04) * mm});
            skLineSegment(sketch, "E351", {"start": v(-1.09, -1.04) * mm, "end": v(-1.09, -1.07) * mm});
            skLineSegment(sketch, "E352", {"start": v(-1.09, -1.07) * mm, "end": v(-1.1, -1.1) * mm});
            skLineSegment(sketch, "E353", {"start": v(-1.1, -1.1) * mm, "end": v(-1.08, -1.13) * mm});
            skLineSegment(sketch, "E354", {"start": v(-1.08, -1.13) * mm, "end": v(-1.04, -1.16) * mm});
            skLineSegment(sketch, "E355", {"start": v(-1.04, -1.16) * mm, "end": v(-1.02, -1.17) * mm});
            skLineSegment(sketch, "E356", {"start": v(-1.02, -1.17) * mm, "end": v(-0.98, -1.17) * mm});
            skLineSegment(sketch, "E357", {"start": v(-0.98, -1.17) * mm, "end": v(-0.95, -1.16) * mm});
            skLineSegment(sketch, "E358", {"start": v(-0.95, -1.16) * mm, "end": v(-0.92, -1.15) * mm});
            skLineSegment(sketch, "E359", {"start": v(-0.92, -1.15) * mm, "end": v(-0.89, -1.15) * mm});
            skLineSegment(sketch, "E360", {"start": v(-0.89, -1.15) * mm, "end": v(-0.86, -1.14) * mm});
            skLineSegment(sketch, "E361", {"start": v(-0.86, -1.14) * mm, "end": v(-0.83, -1.13) * mm});
            skLineSegment(sketch, "E362", {"start": v(-0.83, -1.13) * mm, "end": v(-0.8, -1.12) * mm});
            skLineSegment(sketch, "E363", {"start": v(-0.8, -1.12) * mm, "end": v(-0.79, -1.1) * mm});
            skLineSegment(sketch, "E364", {"start": v(-0.79, -1.1) * mm, "end": v(-0.76, -1.1) * mm});
            skLineSegment(sketch, "E365", {"start": v(-0.76, -1.1) * mm, "end": v(-0.74, -1.1) * mm});
            skLineSegment(sketch, "E366", {"start": v(-0.74, -1.1) * mm, "end": v(-0.72, -1.08) * mm});
            skLineSegment(sketch, "E367", {"start": v(-0.72, -1.08) * mm, "end": v(-0.7, -1.07) * mm});
            skLineSegment(sketch, "E368", {"start": v(-0.7, -1.07) * mm, "end": v(-0.7, -1.06) * mm});
            skLineSegment(sketch, "E369", {"start": v(-0.7, -1.06) * mm, "end": v(-0.68, -1.05) * mm});
            skLineSegment(sketch, "E370", {"start": v(-0.68, -1.05) * mm, "end": v(-0.67, -1.04) * mm});
            skLineSegment(sketch, "E371", {"start": v(-0.67, -1.04) * mm, "end": v(-0.65, -1.03) * mm});
            skLineSegment(sketch, "E372", {"start": v(-0.65, -1.03) * mm, "end": v(-0.64, -1.02) * mm});
            skLineSegment(sketch, "E373", {"start": v(-0.64, -1.02) * mm, "end": v(-0.64, -1.02) * mm});
            skLineSegment(sketch, "E374", {"start": v(-0.64, -1.02) * mm, "end": v(-0.63, -1) * mm});
            skLineSegment(sketch, "E375", {"start": v(-0.63, -1) * mm, "end": v(-0.62, -1) * mm});
            skLineSegment(sketch, "E376", {"start": v(-0.62, -1) * mm, "end": v(-0.62, -1) * mm});
            skLineSegment(sketch, "E377", {"start": v(-0.62, -1) * mm, "end": v(-0.61, -1) * mm});
            skLineSegment(sketch, "E378", {"start": v(-0.61, -1) * mm, "end": v(-0.61, -1) * mm});
            skLineSegment(sketch, "E379", {"start": v(-0.61, -1) * mm, "end": v(-0.61, -0.99) * mm});
            skLineSegment(sketch, "E380", {"start": v(-0.61, -0.99) * mm, "end": v(-0.6, -0.99) * mm});
            skLineSegment(sketch, "E381", {"start": v(-0.6, -0.99) * mm, "end": v(-0.53, -0.85) * mm});
            skLineSegment(sketch, "E382", {"start": v(-0.53, -0.85) * mm, "end": v(-0.3, -0.95) * mm});
            skLineSegment(sketch, "E383", {"start": v(-0.3, -0.95) * mm, "end": v(-0.36, -1.1) * mm});
            skLineSegment(sketch, "E384", {"start": v(-0.36, -1.1) * mm, "end": v(-0.36, -1.1) * mm});
            skLineSegment(sketch, "E385", {"start": v(-0.36, -1.1) * mm, "end": v(-0.36, -1.11) * mm});
            skLineSegment(sketch, "E386", {"start": v(-0.36, -1.11) * mm, "end": v(-0.36, -1.12) * mm});
            skLineSegment(sketch, "E387", {"start": v(-0.36, -1.12) * mm, "end": v(-0.36, -1.12) * mm});
            skLineSegment(sketch, "E388", {"start": v(-0.36, -1.12) * mm, "end": v(-0.36, -1.13) * mm});
            skLineSegment(sketch, "E389", {"start": v(-0.36, -1.13) * mm, "end": v(-0.36, -1.14) * mm});
            skLineSegment(sketch, "E390", {"start": v(-0.36, -1.14) * mm, "end": v(-0.36, -1.15) * mm});
            skLineSegment(sketch, "E391", {"start": v(-0.36, -1.15) * mm, "end": v(-0.36, -1.17) * mm});
            skLineSegment(sketch, "E392", {"start": v(-0.36, -1.17) * mm, "end": v(-0.36, -1.18) * mm});
            skLineSegment(sketch, "E393", {"start": v(-0.36, -1.18) * mm, "end": v(-0.36, -1.2) * mm});
            skLineSegment(sketch, "E394", {"start": v(-0.36, -1.2) * mm, "end": v(-0.36, -1.21) * mm});
            skLineSegment(sketch, "E395", {"start": v(-0.36, -1.21) * mm, "end": v(-0.36, -1.23) * mm});
            skLineSegment(sketch, "E396", {"start": v(-0.36, -1.23) * mm, "end": v(-0.36, -1.25) * mm});
            skLineSegment(sketch, "E397", {"start": v(-0.36, -1.25) * mm, "end": v(-0.35, -1.27) * mm});
            skLineSegment(sketch, "E398", {"start": v(-0.35, -1.27) * mm, "end": v(-0.35, -1.3) * mm});
            skLineSegment(sketch, "E399", {"start": v(-0.35, -1.3) * mm, "end": v(-0.34, -1.32) * mm});
            skLineSegment(sketch, "E400", {"start": v(-0.34, -1.32) * mm, "end": v(-0.33, -1.34) * mm});
            skLineSegment(sketch, "E401", {"start": v(-0.33, -1.34) * mm, "end": v(-0.32, -1.37) * mm});
            skLineSegment(sketch, "E402", {"start": v(-0.32, -1.37) * mm, "end": v(-0.31, -1.4) * mm});
            skLineSegment(sketch, "E403", {"start": v(-0.31, -1.4) * mm, "end": v(-0.3, -1.42) * mm});
            skLineSegment(sketch, "E404", {"start": v(-0.3, -1.42) * mm, "end": v(-0.29, -1.45) * mm});
            skLineSegment(sketch, "E405", {"start": v(-0.29, -1.45) * mm, "end": v(-0.27, -1.48) * mm});
            skLineSegment(sketch, "E406", {"start": v(-0.27, -1.48) * mm, "end": v(-0.25, -1.5) * mm});
            skLineSegment(sketch, "E407", {"start": v(-0.25, -1.5) * mm, "end": v(-0.23, -1.54) * mm});
            skLineSegment(sketch, "E408", {"start": v(-0.23, -1.54) * mm, "end": v(-0.21, -1.55) * mm});
            skLineSegment(sketch, "E409", {"start": v(-0.21, -1.55) * mm, "end": v(-0.16, -1.55) * mm});
            skLineSegment(sketch, "E410", {"start": v(-0.16, -1.55) * mm, "end": v(-0.14, -1.55) * mm});
            skLineSegment(sketch, "E411", {"start": v(-0.14, -1.55) * mm, "end": v(-0.11, -1.52) * mm});
            skLineSegment(sketch, "E412", {"start": v(-0.11, -1.52) * mm, "end": v(-0.09, -1.5) * mm});
            skLineSegment(sketch, "E413", {"start": v(-0.09, -1.5) * mm, "end": v(-0.07, -1.47) * mm});
            skLineSegment(sketch, "E414", {"start": v(-0.07, -1.47) * mm, "end": v(-0.05, -1.45) * mm});
            skLineSegment(sketch, "E415", {"start": v(-0.05, -1.45) * mm, "end": v(-0.03, -1.43) * mm});
            skLineSegment(sketch, "E416", {"start": v(-0.03, -1.43) * mm, "end": v(-0.01, -1.4) * mm});
            skLineSegment(sketch, "E417", {"start": v(-0.01, -1.4) * mm, "end": v(0, -1.38) * mm});
            skLineSegment(sketch, "E418", {"start": v(0, -1.38) * mm, "end": v(0.02, -1.36) * mm});
            skLineSegment(sketch, "E419", {"start": v(0.02, -1.36) * mm, "end": v(0.03, -1.34) * mm});
            skLineSegment(sketch, "E420", {"start": v(0.03, -1.34) * mm, "end": v(0.04, -1.32) * mm});
            skLineSegment(sketch, "E421", {"start": v(0.04, -1.32) * mm, "end": v(0.05, -1.3) * mm});
            skLineSegment(sketch, "E422", {"start": v(0.05, -1.3) * mm, "end": v(0.06, -1.28) * mm});
            skLineSegment(sketch, "E423", {"start": v(0.06, -1.28) * mm, "end": v(0.06, -1.26) * mm});
            skLineSegment(sketch, "E424", {"start": v(0.06, -1.26) * mm, "end": v(0.07, -1.25) * mm});
            skLineSegment(sketch, "E425", {"start": v(0.07, -1.25) * mm, "end": v(0.07, -1.23) * mm});
            skLineSegment(sketch, "E426", {"start": v(0.07, -1.23) * mm, "end": v(0.08, -1.22) * mm});
            skLineSegment(sketch, "E427", {"start": v(0.08, -1.22) * mm, "end": v(0.08, -1.2) * mm});
            skLineSegment(sketch, "E428", {"start": v(0.08, -1.2) * mm, "end": v(0.08, -1.2) * mm});
            skLineSegment(sketch, "E429", {"start": v(0.08, -1.2) * mm, "end": v(0.08, -1.19) * mm});
            skLineSegment(sketch, "E430", {"start": v(0.08, -1.19) * mm, "end": v(0.09, -1.18) * mm});
            skLineSegment(sketch, "E431", {"start": v(0.09, -1.18) * mm, "end": v(0.09, -1.17) * mm});
            skLineSegment(sketch, "E432", {"start": v(0.09, -1.17) * mm, "end": v(0.09, -1.17) * mm});
            skLineSegment(sketch, "E433", {"start": v(0.09, -1.17) * mm, "end": v(0.09, -1.16) * mm});
            skLineSegment(sketch, "E434", {"start": v(0.09, -1.16) * mm, "end": v(0.09, -1.16) * mm});
            skLineSegment(sketch, "E435", {"start": v(0.09, -1.16) * mm, "end": v(0.08, -1) * mm});
            skLineSegment(sketch, "E436", {"start": v(0.08, -1) * mm, "end": v(0.3, -0.95) * mm});
            skLineSegment(sketch, "E437", {"start": v(0.3, -0.95) * mm, "end": v(0.36, -1.1) * mm});
            skLineSegment(sketch, "E438", {"start": v(0.36, -1.1) * mm, "end": v(0.36, -1.1) * mm});
            skLineSegment(sketch, "E439", {"start": v(0.36, -1.1) * mm, "end": v(0.36, -1.11) * mm});
            skLineSegment(sketch, "E440", {"start": v(0.36, -1.11) * mm, "end": v(0.36, -1.12) * mm});
            skLineSegment(sketch, "E441", {"start": v(0.36, -1.12) * mm, "end": v(0.37, -1.12) * mm});
            skLineSegment(sketch, "E442", {"start": v(0.37, -1.12) * mm, "end": v(0.37, -1.13) * mm});
            skLineSegment(sketch, "E443", {"start": v(0.37, -1.13) * mm, "end": v(0.38, -1.14) * mm});
            skLineSegment(sketch, "E444", {"start": v(0.38, -1.14) * mm, "end": v(0.38, -1.15) * mm});
            skLineSegment(sketch, "E445", {"start": v(0.38, -1.15) * mm, "end": v(0.4, -1.16) * mm});
            skLineSegment(sketch, "E446", {"start": v(0.4, -1.16) * mm, "end": v(0.4, -1.17) * mm});
            skLineSegment(sketch, "E447", {"start": v(0.4, -1.17) * mm, "end": v(0.4, -1.18) * mm});
            skLineSegment(sketch, "E448", {"start": v(0.4, -1.18) * mm, "end": v(0.42, -1.2) * mm});
            skLineSegment(sketch, "E449", {"start": v(0.42, -1.2) * mm, "end": v(0.43, -1.2) * mm});
            skLineSegment(sketch, "E450", {"start": v(0.43, -1.2) * mm, "end": v(0.45, -1.22) * mm});
            skLineSegment(sketch, "E451", {"start": v(0.45, -1.22) * mm, "end": v(0.46, -1.23) * mm});
            skLineSegment(sketch, "E452", {"start": v(0.46, -1.23) * mm, "end": v(0.48, -1.25) * mm});
            skLineSegment(sketch, "E453", {"start": v(0.48, -1.25) * mm, "end": v(0.5, -1.26) * mm});
            skLineSegment(sketch, "E454", {"start": v(0.5, -1.26) * mm, "end": v(0.52, -1.28) * mm});
            skLineSegment(sketch, "E455", {"start": v(0.52, -1.28) * mm, "end": v(0.54, -1.3) * mm});
            skLineSegment(sketch, "E456", {"start": v(0.54, -1.3) * mm, "end": v(0.57, -1.3) * mm});
            skLineSegment(sketch, "E457", {"start": v(0.57, -1.3) * mm, "end": v(0.6, -1.32) * mm});
            skLineSegment(sketch, "E458", {"start": v(0.6, -1.32) * mm, "end": v(0.62, -1.34) * mm});
            skLineSegment(sketch, "E459", {"start": v(0.62, -1.34) * mm, "end": v(0.65, -1.35) * mm});
            skLineSegment(sketch, "E460", {"start": v(0.65, -1.35) * mm, "end": v(0.68, -1.37) * mm});
            skLineSegment(sketch, "E461", {"start": v(0.68, -1.37) * mm, "end": v(0.71, -1.38) * mm});
            skLineSegment(sketch, "E462", {"start": v(0.71, -1.38) * mm, "end": v(0.74, -1.38) * mm});
            skLineSegment(sketch, "E463", {"start": v(0.74, -1.38) * mm, "end": v(0.78, -1.35) * mm});
            skLineSegment(sketch, "E464", {"start": v(0.78, -1.35) * mm, "end": v(0.8, -1.33) * mm});
            skLineSegment(sketch, "E465", {"start": v(0.8, -1.33) * mm, "end": v(0.8, -1.3) * mm});
            skLineSegment(sketch, "E466", {"start": v(0.8, -1.3) * mm, "end": v(0.81, -1.26) * mm});
            skLineSegment(sketch, "E467", {"start": v(0.81, -1.26) * mm, "end": v(0.81, -1.23) * mm});
            skLineSegment(sketch, "E468", {"start": v(0.81, -1.23) * mm, "end": v(0.82, -1.2) * mm});
            skLineSegment(sketch, "E469", {"start": v(0.82, -1.2) * mm, "end": v(0.82, -1.17) * mm});
            skLineSegment(sketch, "E470", {"start": v(0.82, -1.17) * mm, "end": v(0.82, -1.14) * mm});
            skLineSegment(sketch, "E471", {"start": v(0.82, -1.14) * mm, "end": v(0.81, -1.12) * mm});
            skLineSegment(sketch, "E472", {"start": v(0.81, -1.12) * mm, "end": v(0.81, -1.09) * mm});
            skLineSegment(sketch, "E473", {"start": v(0.81, -1.09) * mm, "end": v(0.81, -1.07) * mm});
            skLineSegment(sketch, "E474", {"start": v(0.81, -1.07) * mm, "end": v(0.8, -1.04) * mm});
            skLineSegment(sketch, "E475", {"start": v(0.8, -1.04) * mm, "end": v(0.8, -1.02) * mm});
            skLineSegment(sketch, "E476", {"start": v(0.8, -1.02) * mm, "end": v(0.8, -1) * mm});
            skLineSegment(sketch, "E477", {"start": v(0.8, -1) * mm, "end": v(0.8, -0.99) * mm});
            skLineSegment(sketch, "E478", {"start": v(0.8, -0.99) * mm, "end": v(0.79, -0.97) * mm});
            skLineSegment(sketch, "E479", {"start": v(0.79, -0.97) * mm, "end": v(0.78, -0.95) * mm});
            skLineSegment(sketch, "E480", {"start": v(0.78, -0.95) * mm, "end": v(0.78, -0.94) * mm});
            skLineSegment(sketch, "E481", {"start": v(0.78, -0.94) * mm, "end": v(0.78, -0.93) * mm});
            skLineSegment(sketch, "E482", {"start": v(0.78, -0.93) * mm, "end": v(0.77, -0.92) * mm});
            skLineSegment(sketch, "E483", {"start": v(0.77, -0.92) * mm, "end": v(0.77, -0.91) * mm});
            skLineSegment(sketch, "E484", {"start": v(0.77, -0.91) * mm, "end": v(0.76, -0.9) * mm});
            skLineSegment(sketch, "E485", {"start": v(0.76, -0.9) * mm, "end": v(0.76, -0.9) * mm});
            skLineSegment(sketch, "E486", {"start": v(0.76, -0.9) * mm, "end": v(0.75, -0.89) * mm});
            skLineSegment(sketch, "E487", {"start": v(0.75, -0.89) * mm, "end": v(0.75, -0.89) * mm});
            skLineSegment(sketch, "E488", {"start": v(0.75, -0.89) * mm, "end": v(0.75, -0.88) * mm});
            skLineSegment(sketch, "E489", {"start": v(0.75, -0.88) * mm, "end": v(0.65, -0.76) * mm});
            skLineSegment(sketch, "E490", {"start": v(0.65, -0.76) * mm, "end": v(0.81, -0.59) * mm});
            skLineSegment(sketch, "E491", {"start": v(0.81, -0.59) * mm, "end": v(0.94, -0.68) * mm});
            skLineSegment(sketch, "E492", {"start": v(0.94, -0.68) * mm, "end": v(0.94, -0.68) * mm});
            skLineSegment(sketch, "E493", {"start": v(0.94, -0.68) * mm, "end": v(0.95, -0.69) * mm});
            skLineSegment(sketch, "E494", {"start": v(0.95, -0.69) * mm, "end": v(0.95, -0.69) * mm});
            skLineSegment(sketch, "E495", {"start": v(0.95, -0.69) * mm, "end": v(0.96, -0.7) * mm});
            skLineSegment(sketch, "E496", {"start": v(0.96, -0.7) * mm, "end": v(0.97, -0.7) * mm});
            skLineSegment(sketch, "E497", {"start": v(0.97, -0.7) * mm, "end": v(0.97, -0.7) * mm});
            skLineSegment(sketch, "E498", {"start": v(0.97, -0.7) * mm, "end": v(0.98, -0.7) * mm});
            skLineSegment(sketch, "E499", {"start": v(0.98, -0.7) * mm, "end": v(1, -0.7) * mm});
            skLineSegment(sketch, "E500", {"start": v(1, -0.7) * mm, "end": v(1.01, -0.71) * mm});
            skLineSegment(sketch, "E501", {"start": v(1.01, -0.71) * mm, "end": v(1.03, -0.71) * mm});
            skLineSegment(sketch, "E502", {"start": v(1.03, -0.71) * mm, "end": v(1.04, -0.72) * mm});
            skLineSegment(sketch, "E503", {"start": v(1.04, -0.72) * mm, "end": v(1.06, -0.72) * mm});
            skLineSegment(sketch, "E504", {"start": v(1.06, -0.72) * mm, "end": v(1.08, -0.72) * mm});
            skLineSegment(sketch, "E505", {"start": v(1.08, -0.72) * mm, "end": v(1.1, -0.73) * mm});
            skLineSegment(sketch, "E506", {"start": v(1.1, -0.73) * mm, "end": v(1.12, -0.73) * mm});
            skLineSegment(sketch, "E507", {"start": v(1.12, -0.73) * mm, "end": v(1.15, -0.73) * mm});
            skLineSegment(sketch, "E508", {"start": v(1.15, -0.73) * mm, "end": v(1.17, -0.73) * mm});
            skLineSegment(sketch, "E509", {"start": v(1.17, -0.73) * mm, "end": v(1.2, -0.73) * mm});
            skLineSegment(sketch, "E510", {"start": v(1.2, -0.73) * mm, "end": v(1.23, -0.73) * mm});
            skLineSegment(sketch, "E511", {"start": v(1.23, -0.73) * mm, "end": v(1.26, -0.72) * mm});
            skLineSegment(sketch, "E512", {"start": v(1.26, -0.72) * mm, "end": v(1.29, -0.72) * mm});
            skLineSegment(sketch, "E513", {"start": v(1.29, -0.72) * mm, "end": v(1.32, -0.71) * mm});
            skLineSegment(sketch, "E514", {"start": v(1.32, -0.71) * mm, "end": v(1.35, -0.7) * mm});
            skLineSegment(sketch, "E515", {"start": v(1.35, -0.7) * mm, "end": v(1.39, -0.7) * mm});
            skLineSegment(sketch, "E516", {"start": v(1.39, -0.7) * mm, "end": v(1.4, -0.68) * mm});
            skLineSegment(sketch, "E517", {"start": v(1.4, -0.68) * mm, "end": v(1.43, -0.63) * mm});
            skLineSegment(sketch, "E518", {"start": v(1.43, -0.63) * mm, "end": v(1.43, -0.6) * mm});
            skLineSegment(sketch, "E519", {"start": v(1.43, -0.6) * mm, "end": v(1.41, -0.58) * mm});
            skLineSegment(sketch, "E520", {"start": v(1.41, -0.58) * mm, "end": v(1.4, -0.55) * mm});
            skLineSegment(sketch, "E521", {"start": v(1.4, -0.55) * mm, "end": v(1.38, -0.52) * mm});
            skLineSegment(sketch, "E522", {"start": v(1.38, -0.52) * mm, "end": v(1.36, -0.5) * mm});
            skLineSegment(sketch, "E523", {"start": v(1.36, -0.5) * mm, "end": v(1.35, -0.47) * mm});
            skLineSegment(sketch, "E524", {"start": v(1.35, -0.47) * mm, "end": v(1.33, -0.44) * mm});
            skLineSegment(sketch, "E525", {"start": v(1.33, -0.44) * mm, "end": v(1.31, -0.42) * mm});
            skLineSegment(sketch, "E526", {"start": v(1.31, -0.42) * mm, "end": v(1.3, -0.4) * mm});
            skLineSegment(sketch, "E527", {"start": v(1.3, -0.4) * mm, "end": v(1.28, -0.39) * mm});
            skLineSegment(sketch, "E528", {"start": v(1.28, -0.39) * mm, "end": v(1.27, -0.37) * mm});
            skLineSegment(sketch, "E529", {"start": v(1.27, -0.37) * mm, "end": v(1.25, -0.36) * mm});
            skLineSegment(sketch, "E530", {"start": v(1.25, -0.36) * mm, "end": v(1.24, -0.34) * mm});
            skLineSegment(sketch, "E531", {"start": v(1.24, -0.34) * mm, "end": v(1.22, -0.33) * mm});
            skLineSegment(sketch, "E532", {"start": v(1.22, -0.33) * mm, "end": v(1.2, -0.32) * mm});
            skLineSegment(sketch, "E533", {"start": v(1.2, -0.32) * mm, "end": v(1.2, -0.31) * mm});
            skLineSegment(sketch, "E534", {"start": v(1.2, -0.31) * mm, "end": v(1.18, -0.3) * mm});
            skLineSegment(sketch, "E535", {"start": v(1.18, -0.3) * mm, "end": v(1.17, -0.3) * mm});
            skLineSegment(sketch, "E536", {"start": v(1.17, -0.3) * mm, "end": v(1.16, -0.3) * mm});
            skLineSegment(sketch, "E537", {"start": v(1.16, -0.3) * mm, "end": v(1.15, -0.29) * mm});
            skLineSegment(sketch, "E538", {"start": v(1.15, -0.29) * mm, "end": v(1.15, -0.28) * mm});
            skLineSegment(sketch, "E539", {"start": v(1.15, -0.28) * mm, "end": v(1.14, -0.28) * mm});
            skLineSegment(sketch, "E540", {"start": v(1.14, -0.28) * mm, "end": v(1.14, -0.28) * mm});
            skLineSegment(sketch, "E541", {"start": v(1.14, -0.28) * mm, "end": v(1.13, -0.28) * mm});
            skLineSegment(sketch, "E542", {"start": v(1.13, -0.28) * mm, "end": v(1.13, -0.28) * mm});
            skLineSegment(sketch, "E543", {"start": v(1.13, -0.28) * mm, "end": v(1.13, -0.27) * mm});
            skLineSegment(sketch, "E544", {"start": v(1.13, -0.27) * mm, "end": v(0.97, -0.24) * mm});
            skLineSegment(sketch, "E545", {"start": v(0.97, -0.24) * mm, "end": v(1, 0) * mm});
            skLineSegment(sketch, "E546", {"start": v(-0.74, 1.38) * mm, "end": v(-0.78, 1.35) * mm});
            skLineSegment(sketch, "E547", {"start": v(0.1, 0) * mm, "end": v(-0.1, 0) * mm});
            skLineSegment(sketch, "E548", {"start": v(0, -0.1) * mm, "end": v(0, 0.1) * mm});
            skLineSegment(sketch, "E549", {"start": v(1.38, 0.25) * mm, "end": v(1.38, 0.24) * mm});
            skLineSegment(sketch, "E550", {"start": v(1.38, 0.24) * mm, "end": v(1.37, 0.21) * mm});
            skLineSegment(sketch, "E551", {"start": v(1.37, 0.21) * mm, "end": v(1.35, 0.18) * mm});
            skLineSegment(sketch, "E552", {"start": v(1.35, 0.18) * mm, "end": v(1.32, 0.16) * mm});
            skLineSegment(sketch, "E553", {"start": v(1.32, 0.16) * mm, "end": v(1.29, 0.15) * mm});
            skLineSegment(sketch, "E554", {"start": v(1.29, 0.15) * mm, "end": v(1.28, 0.15) * mm});
            skLineSegment(sketch, "E555", {"start": v(1.28, 0.15) * mm, "end": v(1.27, 0.15) * mm});
            skLineSegment(sketch, "E556", {"start": v(1.27, 0.15) * mm, "end": v(1.24, 0.16) * mm});
            skLineSegment(sketch, "E557", {"start": v(1.24, 0.16) * mm, "end": v(1.2, 0.18) * mm});
            skLineSegment(sketch, "E558", {"start": v(1.2, 0.18) * mm, "end": v(1.18, 0.21) * mm});
            skLineSegment(sketch, "E559", {"start": v(1.18, 0.21) * mm, "end": v(1.18, 0.24) * mm});
            skLineSegment(sketch, "E560", {"start": v(1.18, 0.24) * mm, "end": v(1.18, 0.25) * mm});
            skLineSegment(sketch, "E561", {"start": v(1.18, 0.25) * mm, "end": v(1.18, 0.26) * mm});
            skLineSegment(sketch, "E562", {"start": v(1.18, 0.26) * mm, "end": v(1.18, 0.3) * mm});
            skLineSegment(sketch, "E563", {"start": v(1.18, 0.3) * mm, "end": v(1.2, 0.32) * mm});
            skLineSegment(sketch, "E564", {"start": v(1.2, 0.32) * mm, "end": v(1.24, 0.35) * mm});
            skLineSegment(sketch, "E565", {"start": v(1.24, 0.35) * mm, "end": v(1.27, 0.35) * mm});
            skLineSegment(sketch, "E566", {"start": v(1.27, 0.35) * mm, "end": v(1.28, 0.35) * mm});
            skLineSegment(sketch, "E567", {"start": v(1.28, 0.35) * mm, "end": v(1.29, 0.35) * mm});
            skLineSegment(sketch, "E568", {"start": v(1.29, 0.35) * mm, "end": v(1.32, 0.35) * mm});
            skLineSegment(sketch, "E569", {"start": v(1.32, 0.35) * mm, "end": v(1.35, 0.32) * mm});
            skLineSegment(sketch, "E570", {"start": v(1.35, 0.32) * mm, "end": v(1.37, 0.3) * mm});
            skLineSegment(sketch, "E571", {"start": v(1.37, 0.3) * mm, "end": v(1.38, 0.26) * mm});
            skLineSegment(sketch, "E572", {"start": v(1.38, 0.26) * mm, "end": v(1.38, 0.25) * mm});
            skLineSegment(sketch, "E573", {"start": v(-0.52, 0.56) * mm, "end": v(-0.53, 0.55) * mm});
            skLineSegment(sketch, "E574", {"start": v(-0.53, 0.55) * mm, "end": v(-0.55, 0.53) * mm});
            skLineSegment(sketch, "E575", {"start": v(-0.55, 0.53) * mm, "end": v(-0.57, 0.51) * mm});
            skLineSegment(sketch, "E576", {"start": v(-0.57, 0.51) * mm, "end": v(-0.58, 0.5) * mm});
            skLineSegment(sketch, "E577", {"start": v(-0.52, 0.5) * mm, "end": v(-0.58, 0.56) * mm});
            skLineSegment(sketch, "E578", {"start": v(-0.55, 0.6) * mm, "end": v(-0.55, 0.56) * mm});
            skLineSegment(sketch, "E579", {"start": v(-0.55, 0.56) * mm, "end": v(-0.55, 0.53) * mm});
            skLineSegment(sketch, "E580", {"start": v(-0.55, 0.53) * mm, "end": v(-0.55, 0.5) * mm});
            skLineSegment(sketch, "E581", {"start": v(-0.55, 0.5) * mm, "end": v(-0.55, 0.46) * mm});
            skLineSegment(sketch, "E582", {"start": v(-0.48, 0.53) * mm, "end": v(-0.52, 0.53) * mm});
            skLineSegment(sketch, "E583", {"start": v(-0.52, 0.53) * mm, "end": v(-0.55, 0.53) * mm});
            skLineSegment(sketch, "E584", {"start": v(-0.55, 0.53) * mm, "end": v(-0.58, 0.53) * mm});
            skLineSegment(sketch, "E585", {"start": v(-0.58, 0.53) * mm, "end": v(-0.62, 0.53) * mm});
            skLineSegment(sketch, "E586", {"start": v(-0.4, 0.6) * mm, "end": v(-0.4, 0.56) * mm});
            skLineSegment(sketch, "E587", {"start": v(-0.4, 0.56) * mm, "end": v(-0.42, 0.55) * mm});
            skLineSegment(sketch, "E588", {"start": v(-0.42, 0.55) * mm, "end": v(-0.45, 0.56) * mm});
            skLineSegment(sketch, "E589", {"start": v(-0.45, 0.56) * mm, "end": v(-0.5, 0.63) * mm});
            skLineSegment(sketch, "E590", {"start": v(-0.5, 0.63) * mm, "end": v(-0.5, 0.67) * mm});
            skLineSegment(sketch, "E591", {"start": v(-0.5, 0.67) * mm, "end": v(-0.48, 0.68) * mm});
            skLineSegment(sketch, "E592", {"start": v(-0.48, 0.68) * mm, "end": v(-0.45, 0.68) * mm});
            skLineSegment(sketch, "E593", {"start": v(-0.45, 0.68) * mm, "end": v(-0.4, 0.6) * mm});
            skLineSegment(sketch, "E594", {"start": v(-0.2, 0.81) * mm, "end": v(-0.17, 0.67) * mm});
            skLineSegment(sketch, "E595", {"start": v(-0.17, 0.67) * mm, "end": v(-0.2, 0.7) * mm});
            skLineSegment(sketch, "E596", {"start": v(-0.2, 0.7) * mm, "end": v(-0.23, 0.73) * mm});
            skLineSegment(sketch, "E597", {"start": v(-0.23, 0.73) * mm, "end": v(-0.26, 0.76) * mm});
            skLineSegment(sketch, "E598", {"start": v(-0.26, 0.76) * mm, "end": v(-0.3, 0.78) * mm});
            skLineSegment(sketch, "E599", {"start": v(-0.3, 0.78) * mm, "end": v(-0.25, 0.65) * mm});
            skLineSegment(sketch, "E600", {"start": v(-0.04, 0.79) * mm, "end": v(-0.07, 0.78) * mm});
            skLineSegment(sketch, "E601", {"start": v(-0.07, 0.78) * mm, "end": v(-0.1, 0.78) * mm});
            skLineSegment(sketch, "E602", {"start": v(-0.1, 0.78) * mm, "end": v(-0.12, 0.78) * mm});
            skLineSegment(sketch, "E603", {"start": v(-0.12, 0.78) * mm, "end": v(-0.14, 0.78) * mm});
            skLineSegment(sketch, "E604", {"start": v(-0.04, 0.74) * mm, "end": v(-0.06, 0.74) * mm});
            skLineSegment(sketch, "E605", {"start": v(-0.06, 0.74) * mm, "end": v(-0.09, 0.74) * mm});
            skLineSegment(sketch, "E606", {"start": v(-0.09, 0.74) * mm, "end": v(-0.1, 0.73) * mm});
            skLineSegment(sketch, "E607", {"start": v(-0.1, 0.73) * mm, "end": v(-0.13, 0.73) * mm});
            skLineSegment(sketch, "E608", {"start": v(0, 0.81) * mm, "end": v(0.03, 0.83) * mm});
            skLineSegment(sketch, "E609", {"start": v(0.03, 0.83) * mm, "end": v(0.03, 0.7) * mm});
            skLineSegment(sketch, "E610", {"start": v(0.05, 0.7) * mm, "end": v(0.03, 0.7) * mm});
            skLineSegment(sketch, "E611", {"start": v(0.03, 0.7) * mm, "end": v(0, 0.7) * mm});
            skLineSegment(sketch, "E612", {"start": v(0.16, 0.7) * mm, "end": v(0.13, 0.68) * mm});
            skLineSegment(sketch, "E613", {"start": v(0.13, 0.68) * mm, "end": v(0.11, 0.68) * mm});
            skLineSegment(sketch, "E614", {"start": v(0.11, 0.68) * mm, "end": v(0.1, 0.7) * mm});
            skLineSegment(sketch, "E615", {"start": v(0.1, 0.7) * mm, "end": v(0.1, 0.8) * mm});
            skLineSegment(sketch, "E616", {"start": v(0.1, 0.8) * mm, "end": v(0.14, 0.82) * mm});
            skLineSegment(sketch, "E617", {"start": v(0.14, 0.82) * mm, "end": v(0.16, 0.82) * mm});
            skLineSegment(sketch, "E618", {"start": v(0.16, 0.82) * mm, "end": v(0.18, 0.8) * mm});
            skLineSegment(sketch, "E619", {"start": v(0.18, 0.8) * mm, "end": v(0.16, 0.7) * mm});
            skLineSegment(sketch, "E620", {"start": v(0.33, 0.69) * mm, "end": v(0.35, 0.68) * mm});
            skLineSegment(sketch, "E621", {"start": v(0.35, 0.68) * mm, "end": v(0.37, 0.67) * mm});
            skLineSegment(sketch, "E622", {"start": v(0.37, 0.67) * mm, "end": v(0.4, 0.66) * mm});
            skLineSegment(sketch, "E623", {"start": v(0.4, 0.66) * mm, "end": v(0.43, 0.66) * mm});
            skLineSegment(sketch, "E624", {"start": v(0.43, 0.66) * mm, "end": v(0.44, 0.68) * mm});
            skLineSegment(sketch, "E625", {"start": v(0.44, 0.68) * mm, "end": v(0.43, 0.72) * mm});
            skLineSegment(sketch, "E626", {"start": v(0.43, 0.72) * mm, "end": v(0.4, 0.73) * mm});
            skLineSegment(sketch, "E627", {"start": v(0.4, 0.73) * mm, "end": v(0.38, 0.74) * mm});
            skLineSegment(sketch, "E628", {"start": v(0.38, 0.74) * mm, "end": v(0.36, 0.75) * mm});
            skLineSegment(sketch, "E629", {"start": v(0.36, 0.75) * mm, "end": v(0.3, 0.62) * mm});
            skLineSegment(sketch, "E630", {"start": v(0.4, 0.56) * mm, "end": v(0.47, 0.63) * mm});
            skLineSegment(sketch, "E631", {"start": v(0.48, 0.65) * mm, "end": v(0.5, 0.67) * mm});
            skLineSegment(sketch, "E632", {"start": v(0.52, 0.49) * mm, "end": v(0.5, 0.49) * mm});
            skLineSegment(sketch, "E633", {"start": v(0.5, 0.49) * mm, "end": v(0.5, 0.52) * mm});
            skLineSegment(sketch, "E634", {"start": v(0.5, 0.52) * mm, "end": v(0.57, 0.6) * mm});
            skLineSegment(sketch, "E635", {"start": v(0.58, 0.54) * mm, "end": v(0.56, 0.55) * mm});
            skLineSegment(sketch, "E636", {"start": v(0.56, 0.55) * mm, "end": v(0.54, 0.57) * mm});
            skLineSegment(sketch, "E637", {"start": v(0.54, 0.57) * mm, "end": v(0.52, 0.59) * mm});
            skLineSegment(sketch, "E638", {"start": v(0.52, 0.59) * mm, "end": v(0.5, 0.6) * mm});
            skLineSegment(sketch, "E639", {"start": v(0.59, 0.37) * mm, "end": v(0.57, 0.39) * mm});
            skLineSegment(sketch, "E640", {"start": v(0.57, 0.39) * mm, "end": v(0.56, 0.4) * mm});
            skLineSegment(sketch, "E641", {"start": v(0.56, 0.4) * mm, "end": v(0.55, 0.42) * mm});
            skLineSegment(sketch, "E642", {"start": v(0.55, 0.42) * mm, "end": v(0.55, 0.45) * mm});
            skLineSegment(sketch, "E643", {"start": v(0.55, 0.45) * mm, "end": v(0.6, 0.48) * mm});
            skLineSegment(sketch, "E644", {"start": v(0.6, 0.48) * mm, "end": v(0.62, 0.48) * mm});
            skLineSegment(sketch, "E645", {"start": v(0.62, 0.48) * mm, "end": v(0.64, 0.46) * mm});
            skLineSegment(sketch, "E646", {"start": v(0.64, 0.46) * mm, "end": v(0.65, 0.44) * mm});
            skLineSegment(sketch, "E647", {"start": v(0.65, 0.44) * mm, "end": v(0.67, 0.42) * mm});
            skLineSegment(sketch, "E648", {"start": v(0.65, 0.35) * mm, "end": v(0.68, 0.35) * mm});
            skLineSegment(sketch, "E649", {"start": v(0.68, 0.35) * mm, "end": v(0.71, 0.33) * mm});
            skLineSegment(sketch, "E650", {"start": v(0.71, 0.33) * mm, "end": v(0.72, 0.31) * mm});
            skLineSegment(sketch, "E651", {"start": v(0.72, 0.31) * mm, "end": v(0.71, 0.28) * mm});
            skLineSegment(sketch, "E652", {"start": v(0.71, 0.28) * mm, "end": v(0.64, 0.25) * mm});
            skLineSegment(sketch, "E653", {"start": v(0.6, 0.33) * mm, "end": v(0.73, 0.4) * mm});
            skLineSegment(sketch, "E654", {"start": v(0.68, 0.1) * mm, "end": v(0.69, 0.09) * mm});
            skLineSegment(sketch, "E655", {"start": v(0.69, 0.09) * mm, "end": v(0.69, 0.06) * mm});
            skLineSegment(sketch, "E656", {"start": v(0.69, 0.06) * mm, "end": v(0.7, 0.04) * mm});
            skLineSegment(sketch, "E657", {"start": v(0.7, 0.04) * mm, "end": v(0.72, 0.02) * mm});
            skLineSegment(sketch, "E658", {"start": v(0.72, 0.02) * mm, "end": v(0.81, 0.03) * mm});
            skLineSegment(sketch, "E659", {"start": v(0.81, 0.03) * mm, "end": v(0.83, 0.05) * mm});
            skLineSegment(sketch, "E660", {"start": v(0.83, 0.05) * mm, "end": v(0.83, 0.08) * mm});
            skLineSegment(sketch, "E661", {"start": v(0.83, 0.08) * mm, "end": v(0.83, 0.1) * mm});
            skLineSegment(sketch, "E662", {"start": v(0.83, 0.1) * mm, "end": v(0.83, 0.13) * mm});
            skLineSegment(sketch, "E663", {"start": v(0.83, 0.1) * mm, "end": v(0.69, 0.09) * mm});
            skLineSegment(sketch, "E664", {"start": v(0.78, -0.12) * mm, "end": v(0.78, -0.1) * mm});
            skLineSegment(sketch, "E665", {"start": v(0.78, -0.1) * mm, "end": v(0.78, -0.07) * mm});
            skLineSegment(sketch, "E666", {"start": v(0.78, -0.07) * mm, "end": v(0.79, -0.05) * mm});
            skLineSegment(sketch, "E667", {"start": v(0.79, -0.05) * mm, "end": v(0.79, -0.02) * mm});
            skLineSegment(sketch, "E668", {"start": v(0.73, -0.12) * mm, "end": v(0.73, -0.1) * mm});
            skLineSegment(sketch, "E669", {"start": v(0.73, -0.1) * mm, "end": v(0.74, -0.07) * mm});
            skLineSegment(sketch, "E670", {"start": v(0.74, -0.07) * mm, "end": v(0.74, -0.05) * mm});
            skLineSegment(sketch, "E671", {"start": v(0.74, -0.05) * mm, "end": v(0.74, -0.02) * mm});
            skLineSegment(sketch, "E672", {"start": v(0.65, -0.23) * mm, "end": v(0.66, -0.21) * mm});
            skLineSegment(sketch, "E673", {"start": v(0.66, -0.21) * mm, "end": v(0.67, -0.2) * mm});
            skLineSegment(sketch, "E674", {"start": v(0.67, -0.2) * mm, "end": v(0.67, -0.17) * mm});
            skLineSegment(sketch, "E675", {"start": v(0.67, -0.17) * mm, "end": v(0.68, -0.15) * mm});
            skLineSegment(sketch, "E676", {"start": v(0.68, -0.15) * mm, "end": v(0.72, -0.16) * mm});
            skLineSegment(sketch, "E677", {"start": v(0.72, -0.16) * mm, "end": v(0.74, -0.19) * mm});
            skLineSegment(sketch, "E678", {"start": v(0.74, -0.19) * mm, "end": v(0.73, -0.21) * mm});
            skLineSegment(sketch, "E679", {"start": v(0.73, -0.21) * mm, "end": v(0.73, -0.23) * mm});
            skLineSegment(sketch, "E680", {"start": v(0.73, -0.23) * mm, "end": v(0.74, -0.27) * mm});
            skLineSegment(sketch, "E681", {"start": v(0.74, -0.27) * mm, "end": v(0.76, -0.27) * mm});
            skLineSegment(sketch, "E682", {"start": v(0.76, -0.27) * mm, "end": v(0.8, -0.26) * mm});
            skLineSegment(sketch, "E683", {"start": v(0.8, -0.26) * mm, "end": v(0.8, -0.23) * mm});
            skLineSegment(sketch, "E684", {"start": v(0.8, -0.23) * mm, "end": v(0.8, -0.2) * mm});
            skLineSegment(sketch, "E685", {"start": v(0.8, -0.2) * mm, "end": v(0.8, -0.18) * mm});
            skLineSegment(sketch, "E686", {"start": v(0.66, -0.28) * mm, "end": v(0.64, -0.27) * mm});
            skLineSegment(sketch, "E687", {"start": v(0.7, -0.47) * mm, "end": v(0.7, -0.45) * mm});
            skLineSegment(sketch, "E688", {"start": v(0.7, -0.45) * mm, "end": v(0.72, -0.42) * mm});
            skLineSegment(sketch, "E689", {"start": v(0.72, -0.42) * mm, "end": v(0.73, -0.4) * mm});
            skLineSegment(sketch, "E690", {"start": v(0.73, -0.4) * mm, "end": v(0.75, -0.38) * mm});
            skLineSegment(sketch, "E691", {"start": v(0.75, -0.38) * mm, "end": v(0.7, -0.36) * mm});
            skLineSegment(sketch, "E692", {"start": v(0.7, -0.36) * mm, "end": v(0.7, -0.38) * mm});
            skLineSegment(sketch, "E693", {"start": v(0.7, -0.38) * mm, "end": v(0.68, -0.4) * mm});
            skLineSegment(sketch, "E694", {"start": v(0.68, -0.4) * mm, "end": v(0.67, -0.42) * mm});
            skLineSegment(sketch, "E695", {"start": v(0.67, -0.42) * mm, "end": v(0.63, -0.43) * mm});
            skLineSegment(sketch, "E696", {"start": v(0.63, -0.43) * mm, "end": v(0.6, -0.4) * mm});
            skLineSegment(sketch, "E697", {"start": v(0.6, -0.4) * mm, "end": v(0.59, -0.37) * mm});
            skLineSegment(sketch, "E698", {"start": v(0.59, -0.37) * mm, "end": v(0.6, -0.35) * mm});
            skLineSegment(sketch, "E699", {"start": v(0.6, -0.35) * mm, "end": v(0.6, -0.33) * mm});
            skLineSegment(sketch, "E700", {"start": v(0.6, -0.33) * mm, "end": v(0.64, -0.32) * mm});
            skLineSegment(sketch, "E701", {"start": v(0.53, -0.55) * mm, "end": v(0.5, -0.57) * mm});
            skLineSegment(sketch, "E702", {"start": v(0.5, -0.57) * mm, "end": v(0.49, -0.59) * mm});
            skLineSegment(sketch, "E703", {"start": v(0.49, -0.59) * mm, "end": v(0.47, -0.6) * mm});
            skLineSegment(sketch, "E704", {"start": v(0.47, -0.6) * mm, "end": v(0.47, -0.63) * mm});
            skLineSegment(sketch, "E705", {"start": v(0.47, -0.63) * mm, "end": v(0.48, -0.65) * mm});
            skLineSegment(sketch, "E706", {"start": v(0.48, -0.65) * mm, "end": v(0.52, -0.66) * mm});
            skLineSegment(sketch, "E707", {"start": v(0.52, -0.66) * mm, "end": v(0.54, -0.64) * mm});
            skLineSegment(sketch, "E708", {"start": v(0.54, -0.64) * mm, "end": v(0.56, -0.62) * mm});
            skLineSegment(sketch, "E709", {"start": v(0.56, -0.62) * mm, "end": v(0.57, -0.6) * mm});
            skLineSegment(sketch, "E710", {"start": v(0.57, -0.6) * mm, "end": v(0.48, -0.5) * mm});
            skLineSegment(sketch, "E711", {"start": v(0.34, -0.71) * mm, "end": v(0.36, -0.7) * mm});
            skLineSegment(sketch, "E712", {"start": v(0.36, -0.7) * mm, "end": v(0.38, -0.69) * mm});
            skLineSegment(sketch, "E713", {"start": v(0.38, -0.69) * mm, "end": v(0.4, -0.68) * mm});
            skLineSegment(sketch, "E714", {"start": v(0.4, -0.68) * mm, "end": v(0.43, -0.66) * mm});
            skLineSegment(sketch, "E715", {"start": v(0.32, -0.67) * mm, "end": v(0.34, -0.66) * mm});
            skLineSegment(sketch, "E716", {"start": v(0.34, -0.66) * mm, "end": v(0.36, -0.65) * mm});
            skLineSegment(sketch, "E717", {"start": v(0.36, -0.65) * mm, "end": v(0.38, -0.63) * mm});
            skLineSegment(sketch, "E718", {"start": v(0.38, -0.63) * mm, "end": v(0.4, -0.62) * mm});
            skLineSegment(sketch, "E719", {"start": v(0.19, -0.72) * mm, "end": v(0.21, -0.7) * mm});
            skLineSegment(sketch, "E720", {"start": v(0.21, -0.7) * mm, "end": v(0.23, -0.7) * mm});
            skLineSegment(sketch, "E721", {"start": v(0.23, -0.7) * mm, "end": v(0.26, -0.7) * mm});
            skLineSegment(sketch, "E722", {"start": v(0.26, -0.7) * mm, "end": v(0.28, -0.69) * mm});
            skLineSegment(sketch, "E723", {"start": v(0.28, -0.69) * mm, "end": v(0.27, -0.72) * mm});
            skLineSegment(sketch, "E724", {"start": v(0.27, -0.72) * mm, "end": v(0.25, -0.76) * mm});
            skLineSegment(sketch, "E725", {"start": v(0.25, -0.76) * mm, "end": v(0.24, -0.8) * mm});
            skLineSegment(sketch, "E726", {"start": v(0.24, -0.8) * mm, "end": v(0.2, -0.66) * mm});
            skLineSegment(sketch, "E727", {"start": v(0.03, -0.76) * mm, "end": v(0, -0.76) * mm});
            skLineSegment(sketch, "E728", {"start": v(0, -0.76) * mm, "end": v(-0.02, -0.76) * mm});
            skLineSegment(sketch, "E729", {"start": v(-0.02, -0.76) * mm, "end": v(-0.04, -0.76) * mm});
            skLineSegment(sketch, "E730", {"start": v(-0.04, -0.76) * mm, "end": v(-0.07, -0.78) * mm});
            skLineSegment(sketch, "E731", {"start": v(-0.07, -0.78) * mm, "end": v(-0.07, -0.8) * mm});
            skLineSegment(sketch, "E732", {"start": v(-0.07, -0.8) * mm, "end": v(-0.05, -0.83) * mm});
            skLineSegment(sketch, "E733", {"start": v(-0.05, -0.83) * mm, "end": v(-0.02, -0.84) * mm});
            skLineSegment(sketch, "E734", {"start": v(-0.02, -0.84) * mm, "end": v(0, -0.84) * mm});
            skLineSegment(sketch, "E735", {"start": v(0, -0.84) * mm, "end": v(0.03, -0.83) * mm});
            skLineSegment(sketch, "E736", {"start": v(0.03, -0.83) * mm, "end": v(0.03, -0.7) * mm});
            skLineSegment(sketch, "E737", {"start": v(-0.1, -0.68) * mm, "end": v(-0.1, -0.73) * mm});
            skLineSegment(sketch, "E738", {"start": v(-0.1, -0.73) * mm, "end": v(-0.14, -0.78) * mm});
            skLineSegment(sketch, "E739", {"start": v(-0.14, -0.78) * mm, "end": v(-0.17, -0.82) * mm});
            skLineSegment(sketch, "E740", {"start": v(-0.17, -0.82) * mm, "end": v(-0.19, -0.76) * mm});
            skLineSegment(sketch, "E741", {"start": v(-0.19, -0.76) * mm, "end": v(-0.2, -0.71) * mm});
            skLineSegment(sketch, "E742", {"start": v(-0.2, -0.71) * mm, "end": v(-0.19, -0.67) * mm});
            skLineSegment(sketch, "E743", {"start": v(-0.1, -0.73) * mm, "end": v(-0.13, -0.73) * mm});
            skLineSegment(sketch, "E744", {"start": v(-0.13, -0.73) * mm, "end": v(-0.15, -0.72) * mm});
            skLineSegment(sketch, "E745", {"start": v(-0.15, -0.72) * mm, "end": v(-0.18, -0.72) * mm});
            skLineSegment(sketch, "E746", {"start": v(-0.18, -0.72) * mm, "end": v(-0.2, -0.71) * mm});
            skLineSegment(sketch, "E747", {"start": v(-0.35, -0.7) * mm, "end": v(-0.33, -0.72) * mm});
            skLineSegment(sketch, "E748", {"start": v(-0.33, -0.72) * mm, "end": v(-0.3, -0.73) * mm});
            skLineSegment(sketch, "E749", {"start": v(-0.3, -0.73) * mm, "end": v(-0.28, -0.74) * mm});
            skLineSegment(sketch, "E750", {"start": v(-0.28, -0.74) * mm, "end": v(-0.26, -0.74) * mm});
            skLineSegment(sketch, "E751", {"start": v(-0.33, -0.66) * mm, "end": v(-0.3, -0.67) * mm});
            skLineSegment(sketch, "E752", {"start": v(-0.3, -0.67) * mm, "end": v(-0.29, -0.68) * mm});
            skLineSegment(sketch, "E753", {"start": v(-0.29, -0.68) * mm, "end": v(-0.27, -0.7) * mm});
            skLineSegment(sketch, "E754", {"start": v(-0.27, -0.7) * mm, "end": v(-0.24, -0.7) * mm});
            skLineSegment(sketch, "E755", {"start": v(-0.42, -0.55) * mm, "end": v(-0.4, -0.56) * mm});
            skLineSegment(sketch, "E756", {"start": v(-0.4, -0.56) * mm, "end": v(-0.38, -0.58) * mm});
            skLineSegment(sketch, "E757", {"start": v(-0.38, -0.58) * mm, "end": v(-0.36, -0.59) * mm});
            skLineSegment(sketch, "E758", {"start": v(-0.36, -0.59) * mm, "end": v(-0.35, -0.6) * mm});
            skLineSegment(sketch, "E759", {"start": v(-0.35, -0.6) * mm, "end": v(-0.37, -0.64) * mm});
            skLineSegment(sketch, "E760", {"start": v(-0.37, -0.64) * mm, "end": v(-0.4, -0.65) * mm});
            skLineSegment(sketch, "E761", {"start": v(-0.4, -0.65) * mm, "end": v(-0.42, -0.64) * mm});
            skLineSegment(sketch, "E762", {"start": v(-0.42, -0.64) * mm, "end": v(-0.44, -0.62) * mm});
            skLineSegment(sketch, "E763", {"start": v(-0.44, -0.62) * mm, "end": v(-0.48, -0.63) * mm});
            skLineSegment(sketch, "E764", {"start": v(-0.48, -0.63) * mm, "end": v(-0.49, -0.65) * mm});
            skLineSegment(sketch, "E765", {"start": v(-0.49, -0.65) * mm, "end": v(-0.48, -0.68) * mm});
            skLineSegment(sketch, "E766", {"start": v(-0.48, -0.68) * mm, "end": v(-0.46, -0.7) * mm});
            skLineSegment(sketch, "E767", {"start": v(-0.46, -0.7) * mm, "end": v(-0.44, -0.71) * mm});
            skLineSegment(sketch, "E768", {"start": v(-0.44, -0.71) * mm, "end": v(-0.4, -0.7) * mm});
            skLineSegment(sketch, "E769", {"start": v(-0.54, -0.63) * mm, "end": v(-0.56, -0.62) * mm});
            skLineSegment(sketch, "E770", {"start": v(-0.56, -0.62) * mm, "end": v(-0.58, -0.6) * mm});
            skLineSegment(sketch, "E771", {"start": v(-0.58, -0.6) * mm, "end": v(-0.6, -0.58) * mm});
            skLineSegment(sketch, "E772", {"start": v(-0.6, -0.58) * mm, "end": v(-0.62, -0.56) * mm});
            skLineSegment(sketch, "E773", {"start": v(-0.62, -0.56) * mm, "end": v(-0.55, -0.53) * mm});
            skLineSegment(sketch, "E774", {"start": v(-0.55, -0.53) * mm, "end": v(-0.48, -0.5) * mm});
            skSolve(sketch);
        }
        {
            var Q0;
            Q0=makeQuery(id+"F0.imprint","IMPRINT",FACE,{"disambiguationData":[TD([[makeQuery(id+"F0.imprint","IMPRINT",EDGE,{"derivedFrom":sQuery(id+"F0.wireOp",EDGE,"E0")}),-1.0]])]});
            var Q1;
            Q1=makeQuery(id+"F0.imprint","IMPRINT",FACE,{"disambiguationData":[TD([[makeQuery(id+"F0.imprint","IMPRINT",EDGE,{"derivedFrom":sQuery(id+"F0.wireOp",EDGE,"E586")}),-1.0]])]});
            var Q2;
            {var subQ0=sQuery(id+"F0.wireOp",EDGE,"E620");Q2=makeQuery(id+"F0.imprint","IMPRINT",FACE,{"disambiguationData":[TD([[makeQuery(id+"F0.imprint","IMPRINT",EDGE,{"derivedFrom":subQ0}),1.0]])]});}
            var Q3;
            Q3=makeQuery(id+"F0.imprint","IMPRINT",FACE,{"disambiguationData":[TD([[makeQuery(id+"F0.imprint","IMPRINT",EDGE,{"derivedFrom":sQuery(id+"F0.wireOp",EDGE,"E0")}),1.0]])]});
            var Q4;
            Q4=makeQuery(id+"F0.imprint","IMPRINT",FACE,{"disambiguationData":[TD([[makeQuery(id+"F0.imprint","IMPRINT",EDGE,{"derivedFrom":sQuery(id+"F0.wireOp",EDGE,"E549")}),-1.0]])]});
            var Q5;
            Q5=makeQuery(id+"F0.imprint","IMPRINT",FACE,{"disambiguationData":[TD([[makeQuery(id+"F0.imprint","IMPRINT",EDGE,{"derivedFrom":sQuery(id+"F0.wireOp",EDGE,"E655")}),1.0]])]});
            var Q6;
            Q6=makeQuery(id+"F0.imprint","IMPRINT",FACE,{"disambiguationData":[TD([[makeQuery(id+"F0.imprint","IMPRINT",EDGE,{"derivedFrom":sQuery(id+"F0.wireOp",EDGE,"E612")}),-1.0]])]});
            var Q7;
            {var subQ0=sQuery(id+"F0.wireOp",EDGE,"E727");Q7=makeQuery(id+"F0.imprint","IMPRINT",FACE,{"disambiguationData":[TD([[makeQuery(id+"F0.imprint","IMPRINT",EDGE,{"derivedFrom":subQ0}),1.0]])]});}
            var Q8;
            {var subQ0=sQuery(id+"F0.wireOp",EDGE,"E720");Q8=makeQuery(id+"F0.imprint","IMPRINT",FACE,{"disambiguationData":[TD([[makeQuery(id+"F0.imprint","IMPRINT",EDGE,{"derivedFrom":subQ0}),-1.0]])]});}
            var Q9;
            {var subQ0=sQuery(id+"F0.wireOp",EDGE,"E701");Q9=makeQuery(id+"F0.imprint","IMPRINT",FACE,{"disambiguationData":[TD([[makeQuery(id+"F0.imprint","IMPRINT",EDGE,{"derivedFrom":subQ0}),1.0]])]});}
            var Q10;
            Q10=makeQuery(id+"F0.imprint","IMPRINT",FACE,{"disambiguationData":[TD([[makeQuery(id+"F0.imprint","IMPRINT",EDGE,{"derivedFrom":sQuery(id+"F0.wireOp",EDGE,"E738")}),-1.0]])]});
            extrude(context, id + "F1", {"entities" : qUnion([Q0, Q1, Q2, Q3, Q4, Q5, Q6, Q7, Q8, Q9, Q10]), "depth" : 2 * mm, "offsetDistance" : 25 * mm});
        }
        {
            var Q0;
            Q0=makeQuery(id+"F1.opExtrude","SWEPT_BODY",BODY,{"disambiguationData":[OSD([sQuery(id+"F0.wireOp",EDGE,"E0"),sQuery(id+"F0.wireOp",EDGE,"E1"),sQuery(id+"F0.wireOp",EDGE,"E1"),sQuery(id+"F0.wireOp",EDGE,"E2"),sQuery(id+"F0.wireOp",EDGE,"E3"),sQuery(id+"F0.wireOp",EDGE,"E4"),sQuery(id+"F0.wireOp",EDGE,"E5"),sQuery(id+"F0.wireOp",EDGE,"E6"),sQuery(id+"F0.wireOp",EDGE,"E7"),sQuery(id+"F0.wireOp",EDGE,"E8"),sQuery(id+"F0.wireOp",EDGE,"E9"),sQuery(id+"F0.wireOp",EDGE,"E10"),sQuery(id+"F0.wireOp",EDGE,"E11"),sQuery(id+"F0.wireOp",EDGE,"E12"),sQuery(id+"F0.wireOp",EDGE,"E13"),sQuery(id+"F0.wireOp",EDGE,"E14"),sQuery(id+"F0.wireOp",EDGE,"E15"),sQuery(id+"F0.wireOp",EDGE,"E16"),sQuery(id+"F0.wireOp",EDGE,"E17"),sQuery(id+"F0.wireOp",EDGE,"E18"),sQuery(id+"F0.wireOp",EDGE,"E19"),sQuery(id+"F0.wireOp",EDGE,"E20"),sQuery(id+"F0.wireOp",EDGE,"E21"),sQuery(id+"F0.wireOp",EDGE,"E22"),sQuery(id+"F0.wireOp",EDGE,"E23"),sQuery(id+"F0.wireOp",EDGE,"E24"),sQuery(id+"F0.wireOp",EDGE,"E25"),sQuery(id+"F0.wireOp",EDGE,"E26"),sQuery(id+"F0.wireOp",EDGE,"E27"),sQuery(id+"F0.wireOp",EDGE,"E28"),sQuery(id+"F0.wireOp",EDGE,"E29"),sQuery(id+"F0.wireOp",EDGE,"E30"),sQuery(id+"F0.wireOp",EDGE,"E31"),sQuery(id+"F0.wireOp",EDGE,"E32"),sQuery(id+"F0.wireOp",EDGE,"E33"),sQuery(id+"F0.wireOp",EDGE,"E34"),sQuery(id+"F0.wireOp",EDGE,"E35"),sQuery(id+"F0.wireOp",EDGE,"E36"),sQuery(id+"F0.wireOp",EDGE,"E37"),sQuery(id+"F0.wireOp",EDGE,"E38"),sQuery(id+"F0.wireOp",EDGE,"E39"),sQuery(id+"F0.wireOp",EDGE,"E40"),sQuery(id+"F0.wireOp",EDGE,"E41"),sQuery(id+"F0.wireOp",EDGE,"E42"),sQuery(id+"F0.wireOp",EDGE,"E43"),sQuery(id+"F0.wireOp",EDGE,"E44"),sQuery(id+"F0.wireOp",EDGE,"E45"),sQuery(id+"F0.wireOp",EDGE,"E46"),sQuery(id+"F0.wireOp",EDGE,"E47"),sQuery(id+"F0.wireOp",EDGE,"E48"),sQuery(id+"F0.wireOp",EDGE,"E49"),sQuery(id+"F0.wireOp",EDGE,"E50"),sQuery(id+"F0.wireOp",EDGE,"E51"),sQuery(id+"F0.wireOp",EDGE,"E52"),sQuery(id+"F0.wireOp",EDGE,"E53"),sQuery(id+"F0.wireOp",EDGE,"E54"),sQuery(id+"F0.wireOp",EDGE,"E55"),sQuery(id+"F0.wireOp",EDGE,"E56"),sQuery(id+"F0.wireOp",EDGE,"E56"),sQuery(id+"F0.wireOp",EDGE,"E57"),sQuery(id+"F0.wireOp",EDGE,"E58"),sQuery(id+"F0.wireOp",EDGE,"E59"),sQuery(id+"F0.wireOp",EDGE,"E60"),sQuery(id+"F0.wireOp",EDGE,"E61"),sQuery(id+"F0.wireOp",EDGE,"E62"),sQuery(id+"F0.wireOp",EDGE,"E63"),sQuery(id+"F0.wireOp",EDGE,"E64"),sQuery(id+"F0.wireOp",EDGE,"E65"),sQuery(id+"F0.wireOp",EDGE,"E66"),sQuery(id+"F0.wireOp",EDGE,"E67"),sQuery(id+"F0.wireOp",EDGE,"E68"),sQuery(id+"F0.wireOp",EDGE,"E69"),sQuery(id+"F0.wireOp",EDGE,"E70"),sQuery(id+"F0.wireOp",EDGE,"E71"),sQuery(id+"F0.wireOp",EDGE,"E72"),sQuery(id+"F0.wireOp",EDGE,"E73"),sQuery(id+"F0.wireOp",EDGE,"E74"),sQuery(id+"F0.wireOp",EDGE,"E75"),sQuery(id+"F0.wireOp",EDGE,"E76"),sQuery(id+"F0.wireOp",EDGE,"E77"),sQuery(id+"F0.wireOp",EDGE,"E78"),sQuery(id+"F0.wireOp",EDGE,"E79"),sQuery(id+"F0.wireOp",EDGE,"E80"),sQuery(id+"F0.wireOp",EDGE,"E81"),sQuery(id+"F0.wireOp",EDGE,"E82"),sQuery(id+"F0.wireOp",EDGE,"E83"),sQuery(id+"F0.wireOp",EDGE,"E84"),sQuery(id+"F0.wireOp",EDGE,"E85"),sQuery(id+"F0.wireOp",EDGE,"E86"),sQuery(id+"F0.wireOp",EDGE,"E87"),sQuery(id+"F0.wireOp",EDGE,"E88"),sQuery(id+"F0.wireOp",EDGE,"E89"),sQuery(id+"F0.wireOp",EDGE,"E90"),sQuery(id+"F0.wireOp",EDGE,"E91"),sQuery(id+"F0.wireOp",EDGE,"E92"),sQuery(id+"F0.wireOp",EDGE,"E93"),sQuery(id+"F0.wireOp",EDGE,"E94"),sQuery(id+"F0.wireOp",EDGE,"E95"),sQuery(id+"F0.wireOp",EDGE,"E96"),sQuery(id+"F0.wireOp",EDGE,"E97"),sQuery(id+"F0.wireOp",EDGE,"E98"),sQuery(id+"F0.wireOp",EDGE,"E99"),sQuery(id+"F0.wireOp",EDGE,"E100"),sQuery(id+"F0.wireOp",EDGE,"E101"),sQuery(id+"F0.wireOp",EDGE,"E102"),sQuery(id+"F0.wireOp",EDGE,"E103"),sQuery(id+"F0.wireOp",EDGE,"E104"),sQuery(id+"F0.wireOp",EDGE,"E105"),sQuery(id+"F0.wireOp",EDGE,"E106"),sQuery(id+"F0.wireOp",EDGE,"E107"),sQuery(id+"F0.wireOp",EDGE,"E108"),sQuery(id+"F0.wireOp",EDGE,"E109"),sQuery(id+"F0.wireOp",EDGE,"E110"),sQuery(id+"F0.wireOp",EDGE,"E111"),sQuery(id+"F0.wireOp",EDGE,"E111"),sQuery(id+"F0.wireOp",EDGE,"E112"),sQuery(id+"F0.wireOp",EDGE,"E113"),sQuery(id+"F0.wireOp",EDGE,"E114"),sQuery(id+"F0.wireOp",EDGE,"E115"),sQuery(id+"F0.wireOp",EDGE,"E116"),sQuery(id+"F0.wireOp",EDGE,"E117"),sQuery(id+"F0.wireOp",EDGE,"E118"),sQuery(id+"F0.wireOp",EDGE,"E119"),sQuery(id+"F0.wireOp",EDGE,"E120"),sQuery(id+"F0.wireOp",EDGE,"E121"),sQuery(id+"F0.wireOp",EDGE,"E122"),sQuery(id+"F0.wireOp",EDGE,"E123"),sQuery(id+"F0.wireOp",EDGE,"E124"),sQuery(id+"F0.wireOp",EDGE,"E125"),sQuery(id+"F0.wireOp",EDGE,"E126"),sQuery(id+"F0.wireOp",EDGE,"E127"),sQuery(id+"F0.wireOp",EDGE,"E128"),sQuery(id+"F0.wireOp",EDGE,"E129"),sQuery(id+"F0.wireOp",EDGE,"E130"),sQuery(id+"F0.wireOp",EDGE,"E131"),sQuery(id+"F0.wireOp",EDGE,"E132"),sQuery(id+"F0.wireOp",EDGE,"E133"),sQuery(id+"F0.wireOp",EDGE,"E134"),sQuery(id+"F0.wireOp",EDGE,"E135"),sQuery(id+"F0.wireOp",EDGE,"E136"),sQuery(id+"F0.wireOp",EDGE,"E137"),sQuery(id+"F0.wireOp",EDGE,"E138"),sQuery(id+"F0.wireOp",EDGE,"E139"),sQuery(id+"F0.wireOp",EDGE,"E140"),sQuery(id+"F0.wireOp",EDGE,"E141"),sQuery(id+"F0.wireOp",EDGE,"E142"),sQuery(id+"F0.wireOp",EDGE,"E143"),sQuery(id+"F0.wireOp",EDGE,"E144"),sQuery(id+"F0.wireOp",EDGE,"E145"),sQuery(id+"F0.wireOp",EDGE,"E146"),sQuery(id+"F0.wireOp",EDGE,"E147"),sQuery(id+"F0.wireOp",EDGE,"E148"),sQuery(id+"F0.wireOp",EDGE,"E149"),sQuery(id+"F0.wireOp",EDGE,"E150"),sQuery(id+"F0.wireOp",EDGE,"E151"),sQuery(id+"F0.wireOp",EDGE,"E152"),sQuery(id+"F0.wireOp",EDGE,"E153"),sQuery(id+"F0.wireOp",EDGE,"E154"),sQuery(id+"F0.wireOp",EDGE,"E155"),sQuery(id+"F0.wireOp",EDGE,"E156"),sQuery(id+"F0.wireOp",EDGE,"E157"),sQuery(id+"F0.wireOp",EDGE,"E158"),sQuery(id+"F0.wireOp",EDGE,"E159"),sQuery(id+"F0.wireOp",EDGE,"E160"),sQuery(id+"F0.wireOp",EDGE,"E161"),sQuery(id+"F0.wireOp",EDGE,"E161"),sQuery(id+"F0.wireOp",EDGE,"E162"),sQuery(id+"F0.wireOp",EDGE,"E163"),sQuery(id+"F0.wireOp",EDGE,"E164"),sQuery(id+"F0.wireOp",EDGE,"E165"),sQuery(id+"F0.wireOp",EDGE,"E165"),sQuery(id+"F0.wireOp",EDGE,"E166"),sQuery(id+"F0.wireOp",EDGE,"E167"),sQuery(id+"F0.wireOp",EDGE,"E168"),sQuery(id+"F0.wireOp",EDGE,"E169"),sQuery(id+"F0.wireOp",EDGE,"E170"),sQuery(id+"F0.wireOp",EDGE,"E171"),sQuery(id+"F0.wireOp",EDGE,"E172"),sQuery(id+"F0.wireOp",EDGE,"E173"),sQuery(id+"F0.wireOp",EDGE,"E174"),sQuery(id+"F0.wireOp",EDGE,"E175"),sQuery(id+"F0.wireOp",EDGE,"E176"),sQuery(id+"F0.wireOp",EDGE,"E177"),sQuery(id+"F0.wireOp",EDGE,"E178"),sQuery(id+"F0.wireOp",EDGE,"E179"),sQuery(id+"F0.wireOp",EDGE,"E180"),sQuery(id+"F0.wireOp",EDGE,"E181"),sQuery(id+"F0.wireOp",EDGE,"E182"),sQuery(id+"F0.wireOp",EDGE,"E183"),sQuery(id+"F0.wireOp",EDGE,"E184"),sQuery(id+"F0.wireOp",EDGE,"E185"),sQuery(id+"F0.wireOp",EDGE,"E186"),sQuery(id+"F0.wireOp",EDGE,"E187"),sQuery(id+"F0.wireOp",EDGE,"E188"),sQuery(id+"F0.wireOp",EDGE,"E189"),sQuery(id+"F0.wireOp",EDGE,"E546"),sQuery(id+"F0.wireOp",EDGE,"E191"),sQuery(id+"F0.wireOp",EDGE,"E192"),sQuery(id+"F0.wireOp",EDGE,"E193"),sQuery(id+"F0.wireOp",EDGE,"E194"),sQuery(id+"F0.wireOp",EDGE,"E195"),sQuery(id+"F0.wireOp",EDGE,"E196"),sQuery(id+"F0.wireOp",EDGE,"E197"),sQuery(id+"F0.wireOp",EDGE,"E198"),sQuery(id+"F0.wireOp",EDGE,"E199"),sQuery(id+"F0.wireOp",EDGE,"E200"),sQuery(id+"F0.wireOp",EDGE,"E201"),sQuery(id+"F0.wireOp",EDGE,"E202"),sQuery(id+"F0.wireOp",EDGE,"E203"),sQuery(id+"F0.wireOp",EDGE,"E204"),sQuery(id+"F0.wireOp",EDGE,"E205"),sQuery(id+"F0.wireOp",EDGE,"E206"),sQuery(id+"F0.wireOp",EDGE,"E207"),sQuery(id+"F0.wireOp",EDGE,"E208"),sQuery(id+"F0.wireOp",EDGE,"E209"),sQuery(id+"F0.wireOp",EDGE,"E210"),sQuery(id+"F0.wireOp",EDGE,"E211"),sQuery(id+"F0.wireOp",EDGE,"E212"),sQuery(id+"F0.wireOp",EDGE,"E212"),sQuery(id+"F0.wireOp",EDGE,"E213"),sQuery(id+"F0.wireOp",EDGE,"E214"),sQuery(id+"F0.wireOp",EDGE,"E215"),sQuery(id+"F0.wireOp",EDGE,"E216"),sQuery(id+"F0.wireOp",EDGE,"E217"),sQuery(id+"F0.wireOp",EDGE,"E218"),sQuery(id+"F0.wireOp",EDGE,"E219"),sQuery(id+"F0.wireOp",EDGE,"E219"),sQuery(id+"F0.wireOp",EDGE,"E220"),sQuery(id+"F0.wireOp",EDGE,"E221"),sQuery(id+"F0.wireOp",EDGE,"E222"),sQuery(id+"F0.wireOp",EDGE,"E223"),sQuery(id+"F0.wireOp",EDGE,"E224"),sQuery(id+"F0.wireOp",EDGE,"E225"),sQuery(id+"F0.wireOp",EDGE,"E226"),sQuery(id+"F0.wireOp",EDGE,"E227"),sQuery(id+"F0.wireOp",EDGE,"E228"),sQuery(id+"F0.wireOp",EDGE,"E229"),sQuery(id+"F0.wireOp",EDGE,"E230"),sQuery(id+"F0.wireOp",EDGE,"E231"),sQuery(id+"F0.wireOp",EDGE,"E232"),sQuery(id+"F0.wireOp",EDGE,"E233"),sQuery(id+"F0.wireOp",EDGE,"E234"),sQuery(id+"F0.wireOp",EDGE,"E235"),sQuery(id+"F0.wireOp",EDGE,"E236"),sQuery(id+"F0.wireOp",EDGE,"E237"),sQuery(id+"F0.wireOp",EDGE,"E238"),sQuery(id+"F0.wireOp",EDGE,"E239"),sQuery(id+"F0.wireOp",EDGE,"E240"),sQuery(id+"F0.wireOp",EDGE,"E241"),sQuery(id+"F0.wireOp",EDGE,"E242"),sQuery(id+"F0.wireOp",EDGE,"E243"),sQuery(id+"F0.wireOp",EDGE,"E244"),sQuery(id+"F0.wireOp",EDGE,"E245"),sQuery(id+"F0.wireOp",EDGE,"E246"),sQuery(id+"F0.wireOp",EDGE,"E247"),sQuery(id+"F0.wireOp",EDGE,"E248"),sQuery(id+"F0.wireOp",EDGE,"E249"),sQuery(id+"F0.wireOp",EDGE,"E250"),sQuery(id+"F0.wireOp",EDGE,"E251"),sQuery(id+"F0.wireOp",EDGE,"E252"),sQuery(id+"F0.wireOp",EDGE,"E253"),sQuery(id+"F0.wireOp",EDGE,"E254"),sQuery(id+"F0.wireOp",EDGE,"E255"),sQuery(id+"F0.wireOp",EDGE,"E256"),sQuery(id+"F0.wireOp",EDGE,"E257"),sQuery(id+"F0.wireOp",EDGE,"E258"),sQuery(id+"F0.wireOp",EDGE,"E259"),sQuery(id+"F0.wireOp",EDGE,"E260"),sQuery(id+"F0.wireOp",EDGE,"E261"),sQuery(id+"F0.wireOp",EDGE,"E262"),sQuery(id+"F0.wireOp",EDGE,"E263"),sQuery(id+"F0.wireOp",EDGE,"E264"),sQuery(id+"F0.wireOp",EDGE,"E265"),sQuery(id+"F0.wireOp",EDGE,"E266"),sQuery(id+"F0.wireOp",EDGE,"E267"),sQuery(id+"F0.wireOp",EDGE,"E268"),sQuery(id+"F0.wireOp",EDGE,"E269"),sQuery(id+"F0.wireOp",EDGE,"E270"),sQuery(id+"F0.wireOp",EDGE,"E271"),sQuery(id+"F0.wireOp",EDGE,"E272"),sQuery(id+"F0.wireOp",EDGE,"E273"),sQuery(id+"F0.wireOp",EDGE,"E274"),sQuery(id+"F0.wireOp",EDGE,"E274"),sQuery(id+"F0.wireOp",EDGE,"E275"),sQuery(id+"F0.wireOp",EDGE,"E276"),sQuery(id+"F0.wireOp",EDGE,"E277"),sQuery(id+"F0.wireOp",EDGE,"E278"),sQuery(id+"F0.wireOp",EDGE,"E279"),sQuery(id+"F0.wireOp",EDGE,"E280"),sQuery(id+"F0.wireOp",EDGE,"E281"),sQuery(id+"F0.wireOp",EDGE,"E282"),sQuery(id+"F0.wireOp",EDGE,"E283"),sQuery(id+"F0.wireOp",EDGE,"E284"),sQuery(id+"F0.wireOp",EDGE,"E285"),sQuery(id+"F0.wireOp",EDGE,"E286"),sQuery(id+"F0.wireOp",EDGE,"E287"),sQuery(id+"F0.wireOp",EDGE,"E288"),sQuery(id+"F0.wireOp",EDGE,"E289"),sQuery(id+"F0.wireOp",EDGE,"E290"),sQuery(id+"F0.wireOp",EDGE,"E291"),sQuery(id+"F0.wireOp",EDGE,"E292"),sQuery(id+"F0.wireOp",EDGE,"E293"),sQuery(id+"F0.wireOp",EDGE,"E294"),sQuery(id+"F0.wireOp",EDGE,"E295"),sQuery(id+"F0.wireOp",EDGE,"E296"),sQuery(id+"F0.wireOp",EDGE,"E297"),sQuery(id+"F0.wireOp",EDGE,"E298"),sQuery(id+"F0.wireOp",EDGE,"E299"),sQuery(id+"F0.wireOp",EDGE,"E300"),sQuery(id+"F0.wireOp",EDGE,"E301"),sQuery(id+"F0.wireOp",EDGE,"E302"),sQuery(id+"F0.wireOp",EDGE,"E303"),sQuery(id+"F0.wireOp",EDGE,"E304"),sQuery(id+"F0.wireOp",EDGE,"E305"),sQuery(id+"F0.wireOp",EDGE,"E306"),sQuery(id+"F0.wireOp",EDGE,"E307"),sQuery(id+"F0.wireOp",EDGE,"E308"),sQuery(id+"F0.wireOp",EDGE,"E309"),sQuery(id+"F0.wireOp",EDGE,"E310"),sQuery(id+"F0.wireOp",EDGE,"E311"),sQuery(id+"F0.wireOp",EDGE,"E312"),sQuery(id+"F0.wireOp",EDGE,"E313"),sQuery(id+"F0.wireOp",EDGE,"E314"),sQuery(id+"F0.wireOp",EDGE,"E315"),sQuery(id+"F0.wireOp",EDGE,"E316"),sQuery(id+"F0.wireOp",EDGE,"E317"),sQuery(id+"F0.wireOp",EDGE,"E318"),sQuery(id+"F0.wireOp",EDGE,"E319"),sQuery(id+"F0.wireOp",EDGE,"E320"),sQuery(id+"F0.wireOp",EDGE,"E321"),sQuery(id+"F0.wireOp",EDGE,"E322"),sQuery(id+"F0.wireOp",EDGE,"E323"),sQuery(id+"F0.wireOp",EDGE,"E324"),sQuery(id+"F0.wireOp",EDGE,"E325"),sQuery(id+"F0.wireOp",EDGE,"E326"),sQuery(id+"F0.wireOp",EDGE,"E327"),sQuery(id+"F0.wireOp",EDGE,"E328"),sQuery(id+"F0.wireOp",EDGE,"E329"),sQuery(id+"F0.wireOp",EDGE,"E329"),sQuery(id+"F0.wireOp",EDGE,"E330"),sQuery(id+"F0.wireOp",EDGE,"E331"),sQuery(id+"F0.wireOp",EDGE,"E332"),sQuery(id+"F0.wireOp",EDGE,"E333"),sQuery(id+"F0.wireOp",EDGE,"E334"),sQuery(id+"F0.wireOp",EDGE,"E335"),sQuery(id+"F0.wireOp",EDGE,"E336"),sQuery(id+"F0.wireOp",EDGE,"E337"),sQuery(id+"F0.wireOp",EDGE,"E338"),sQuery(id+"F0.wireOp",EDGE,"E339"),sQuery(id+"F0.wireOp",EDGE,"E340"),sQuery(id+"F0.wireOp",EDGE,"E341"),sQuery(id+"F0.wireOp",EDGE,"E342"),sQuery(id+"F0.wireOp",EDGE,"E343"),sQuery(id+"F0.wireOp",EDGE,"E344"),sQuery(id+"F0.wireOp",EDGE,"E345"),sQuery(id+"F0.wireOp",EDGE,"E346"),sQuery(id+"F0.wireOp",EDGE,"E347"),sQuery(id+"F0.wireOp",EDGE,"E348"),sQuery(id+"F0.wireOp",EDGE,"E349"),sQuery(id+"F0.wireOp",EDGE,"E350"),sQuery(id+"F0.wireOp",EDGE,"E351"),sQuery(id+"F0.wireOp",EDGE,"E352"),sQuery(id+"F0.wireOp",EDGE,"E353"),sQuery(id+"F0.wireOp",EDGE,"E354"),sQuery(id+"F0.wireOp",EDGE,"E355"),sQuery(id+"F0.wireOp",EDGE,"E356"),sQuery(id+"F0.wireOp",EDGE,"E357"),sQuery(id+"F0.wireOp",EDGE,"E358"),sQuery(id+"F0.wireOp",EDGE,"E359"),sQuery(id+"F0.wireOp",EDGE,"E360"),sQuery(id+"F0.wireOp",EDGE,"E361"),sQuery(id+"F0.wireOp",EDGE,"E362"),sQuery(id+"F0.wireOp",EDGE,"E363"),sQuery(id+"F0.wireOp",EDGE,"E364"),sQuery(id+"F0.wireOp",EDGE,"E365"),sQuery(id+"F0.wireOp",EDGE,"E366"),sQuery(id+"F0.wireOp",EDGE,"E367"),sQuery(id+"F0.wireOp",EDGE,"E368"),sQuery(id+"F0.wireOp",EDGE,"E369"),sQuery(id+"F0.wireOp",EDGE,"E370"),sQuery(id+"F0.wireOp",EDGE,"E371"),sQuery(id+"F0.wireOp",EDGE,"E372"),sQuery(id+"F0.wireOp",EDGE,"E373"),sQuery(id+"F0.wireOp",EDGE,"E374"),sQuery(id+"F0.wireOp",EDGE,"E375"),sQuery(id+"F0.wireOp",EDGE,"E376"),sQuery(id+"F0.wireOp",EDGE,"E377"),sQuery(id+"F0.wireOp",EDGE,"E378"),sQuery(id+"F0.wireOp",EDGE,"E379"),sQuery(id+"F0.wireOp",EDGE,"E380"),sQuery(id+"F0.wireOp",EDGE,"E381"),sQuery(id+"F0.wireOp",EDGE,"E382"),sQuery(id+"F0.wireOp",EDGE,"E383"),sQuery(id+"F0.wireOp",EDGE,"E384"),sQuery(id+"F0.wireOp",EDGE,"E384"),sQuery(id+"F0.wireOp",EDGE,"E385"),sQuery(id+"F0.wireOp",EDGE,"E386"),sQuery(id+"F0.wireOp",EDGE,"E387"),sQuery(id+"F0.wireOp",EDGE,"E388"),sQuery(id+"F0.wireOp",EDGE,"E389"),sQuery(id+"F0.wireOp",EDGE,"E390"),sQuery(id+"F0.wireOp",EDGE,"E391"),sQuery(id+"F0.wireOp",EDGE,"E392"),sQuery(id+"F0.wireOp",EDGE,"E393"),sQuery(id+"F0.wireOp",EDGE,"E394"),sQuery(id+"F0.wireOp",EDGE,"E395"),sQuery(id+"F0.wireOp",EDGE,"E396"),sQuery(id+"F0.wireOp",EDGE,"E397"),sQuery(id+"F0.wireOp",EDGE,"E398"),sQuery(id+"F0.wireOp",EDGE,"E399"),sQuery(id+"F0.wireOp",EDGE,"E400"),sQuery(id+"F0.wireOp",EDGE,"E401"),sQuery(id+"F0.wireOp",EDGE,"E402"),sQuery(id+"F0.wireOp",EDGE,"E403"),sQuery(id+"F0.wireOp",EDGE,"E404"),sQuery(id+"F0.wireOp",EDGE,"E405"),sQuery(id+"F0.wireOp",EDGE,"E406"),sQuery(id+"F0.wireOp",EDGE,"E407"),sQuery(id+"F0.wireOp",EDGE,"E408"),sQuery(id+"F0.wireOp",EDGE,"E409"),sQuery(id+"F0.wireOp",EDGE,"E410"),sQuery(id+"F0.wireOp",EDGE,"E411"),sQuery(id+"F0.wireOp",EDGE,"E412"),sQuery(id+"F0.wireOp",EDGE,"E413"),sQuery(id+"F0.wireOp",EDGE,"E414"),sQuery(id+"F0.wireOp",EDGE,"E415"),sQuery(id+"F0.wireOp",EDGE,"E416"),sQuery(id+"F0.wireOp",EDGE,"E417"),sQuery(id+"F0.wireOp",EDGE,"E418"),sQuery(id+"F0.wireOp",EDGE,"E419"),sQuery(id+"F0.wireOp",EDGE,"E420"),sQuery(id+"F0.wireOp",EDGE,"E421"),sQuery(id+"F0.wireOp",EDGE,"E422"),sQuery(id+"F0.wireOp",EDGE,"E423"),sQuery(id+"F0.wireOp",EDGE,"E424"),sQuery(id+"F0.wireOp",EDGE,"E425"),sQuery(id+"F0.wireOp",EDGE,"E426"),sQuery(id+"F0.wireOp",EDGE,"E427"),sQuery(id+"F0.wireOp",EDGE,"E428"),sQuery(id+"F0.wireOp",EDGE,"E429"),sQuery(id+"F0.wireOp",EDGE,"E430"),sQuery(id+"F0.wireOp",EDGE,"E431"),sQuery(id+"F0.wireOp",EDGE,"E432"),sQuery(id+"F0.wireOp",EDGE,"E433"),sQuery(id+"F0.wireOp",EDGE,"E434"),sQuery(id+"F0.wireOp",EDGE,"E434"),sQuery(id+"F0.wireOp",EDGE,"E435"),sQuery(id+"F0.wireOp",EDGE,"E436"),sQuery(id+"F0.wireOp",EDGE,"E437"),sQuery(id+"F0.wireOp",EDGE,"E438"),sQuery(id+"F0.wireOp",EDGE,"E438"),sQuery(id+"F0.wireOp",EDGE,"E439"),sQuery(id+"F0.wireOp",EDGE,"E440"),sQuery(id+"F0.wireOp",EDGE,"E441"),sQuery(id+"F0.wireOp",EDGE,"E442"),sQuery(id+"F0.wireOp",EDGE,"E443"),sQuery(id+"F0.wireOp",EDGE,"E444"),sQuery(id+"F0.wireOp",EDGE,"E445"),sQuery(id+"F0.wireOp",EDGE,"E446"),sQuery(id+"F0.wireOp",EDGE,"E447"),sQuery(id+"F0.wireOp",EDGE,"E448"),sQuery(id+"F0.wireOp",EDGE,"E449"),sQuery(id+"F0.wireOp",EDGE,"E450"),sQuery(id+"F0.wireOp",EDGE,"E451"),sQuery(id+"F0.wireOp",EDGE,"E452"),sQuery(id+"F0.wireOp",EDGE,"E453"),sQuery(id+"F0.wireOp",EDGE,"E454"),sQuery(id+"F0.wireOp",EDGE,"E455"),sQuery(id+"F0.wireOp",EDGE,"E456"),sQuery(id+"F0.wireOp",EDGE,"E457"),sQuery(id+"F0.wireOp",EDGE,"E458"),sQuery(id+"F0.wireOp",EDGE,"E459"),sQuery(id+"F0.wireOp",EDGE,"E460"),sQuery(id+"F0.wireOp",EDGE,"E461"),sQuery(id+"F0.wireOp",EDGE,"E462"),sQuery(id+"F0.wireOp",EDGE,"E463"),sQuery(id+"F0.wireOp",EDGE,"E464"),sQuery(id+"F0.wireOp",EDGE,"E465"),sQuery(id+"F0.wireOp",EDGE,"E466"),sQuery(id+"F0.wireOp",EDGE,"E467"),sQuery(id+"F0.wireOp",EDGE,"E468"),sQuery(id+"F0.wireOp",EDGE,"E469"),sQuery(id+"F0.wireOp",EDGE,"E470"),sQuery(id+"F0.wireOp",EDGE,"E471"),sQuery(id+"F0.wireOp",EDGE,"E472"),sQuery(id+"F0.wireOp",EDGE,"E473"),sQuery(id+"F0.wireOp",EDGE,"E474"),sQuery(id+"F0.wireOp",EDGE,"E475"),sQuery(id+"F0.wireOp",EDGE,"E476"),sQuery(id+"F0.wireOp",EDGE,"E477"),sQuery(id+"F0.wireOp",EDGE,"E478"),sQuery(id+"F0.wireOp",EDGE,"E479"),sQuery(id+"F0.wireOp",EDGE,"E480"),sQuery(id+"F0.wireOp",EDGE,"E481"),sQuery(id+"F0.wireOp",EDGE,"E482"),sQuery(id+"F0.wireOp",EDGE,"E483"),sQuery(id+"F0.wireOp",EDGE,"E484"),sQuery(id+"F0.wireOp",EDGE,"E485"),sQuery(id+"F0.wireOp",EDGE,"E485"),sQuery(id+"F0.wireOp",EDGE,"E486"),sQuery(id+"F0.wireOp",EDGE,"E487"),sQuery(id+"F0.wireOp",EDGE,"E488"),sQuery(id+"F0.wireOp",EDGE,"E489"),sQuery(id+"F0.wireOp",EDGE,"E490"),sQuery(id+"F0.wireOp",EDGE,"E491"),sQuery(id+"F0.wireOp",EDGE,"E492"),sQuery(id+"F0.wireOp",EDGE,"E492"),sQuery(id+"F0.wireOp",EDGE,"E493"),sQuery(id+"F0.wireOp",EDGE,"E494"),sQuery(id+"F0.wireOp",EDGE,"E495"),sQuery(id+"F0.wireOp",EDGE,"E496"),sQuery(id+"F0.wireOp",EDGE,"E497"),sQuery(id+"F0.wireOp",EDGE,"E498"),sQuery(id+"F0.wireOp",EDGE,"E499"),sQuery(id+"F0.wireOp",EDGE,"E500"),sQuery(id+"F0.wireOp",EDGE,"E501"),sQuery(id+"F0.wireOp",EDGE,"E502"),sQuery(id+"F0.wireOp",EDGE,"E503"),sQuery(id+"F0.wireOp",EDGE,"E504"),sQuery(id+"F0.wireOp",EDGE,"E505"),sQuery(id+"F0.wireOp",EDGE,"E506"),sQuery(id+"F0.wireOp",EDGE,"E507"),sQuery(id+"F0.wireOp",EDGE,"E508"),sQuery(id+"F0.wireOp",EDGE,"E509"),sQuery(id+"F0.wireOp",EDGE,"E510"),sQuery(id+"F0.wireOp",EDGE,"E511"),sQuery(id+"F0.wireOp",EDGE,"E512"),sQuery(id+"F0.wireOp",EDGE,"E513"),sQuery(id+"F0.wireOp",EDGE,"E514"),sQuery(id+"F0.wireOp",EDGE,"E515"),sQuery(id+"F0.wireOp",EDGE,"E516"),sQuery(id+"F0.wireOp",EDGE,"E517"),sQuery(id+"F0.wireOp",EDGE,"E518"),sQuery(id+"F0.wireOp",EDGE,"E519"),sQuery(id+"F0.wireOp",EDGE,"E520"),sQuery(id+"F0.wireOp",EDGE,"E521"),sQuery(id+"F0.wireOp",EDGE,"E522"),sQuery(id+"F0.wireOp",EDGE,"E523"),sQuery(id+"F0.wireOp",EDGE,"E524"),sQuery(id+"F0.wireOp",EDGE,"E525"),sQuery(id+"F0.wireOp",EDGE,"E526"),sQuery(id+"F0.wireOp",EDGE,"E527"),sQuery(id+"F0.wireOp",EDGE,"E528"),sQuery(id+"F0.wireOp",EDGE,"E529"),sQuery(id+"F0.wireOp",EDGE,"E530"),sQuery(id+"F0.wireOp",EDGE,"E531"),sQuery(id+"F0.wireOp",EDGE,"E532"),sQuery(id+"F0.wireOp",EDGE,"E533"),sQuery(id+"F0.wireOp",EDGE,"E534"),sQuery(id+"F0.wireOp",EDGE,"E535"),sQuery(id+"F0.wireOp",EDGE,"E536"),sQuery(id+"F0.wireOp",EDGE,"E537"),sQuery(id+"F0.wireOp",EDGE,"E538"),sQuery(id+"F0.wireOp",EDGE,"E539"),sQuery(id+"F0.wireOp",EDGE,"E540"),sQuery(id+"F0.wireOp",EDGE,"E541"),sQuery(id+"F0.wireOp",EDGE,"E542"),sQuery(id+"F0.wireOp",EDGE,"E543"),sQuery(id+"F0.wireOp",EDGE,"E544"),sQuery(id+"F0.wireOp",EDGE,"E545")])]});
            var Q1;
            Q1=qCreatedBy(makeId("Origin.pointOp"),VERTEX);
            transform(context, id + "F2", {"entities" : qUnion([Q0]), "transformType" : TransformType.SCALE_UNIFORMLY, "scale" : 3.19, "scalePoint" : qUnion([Q1]), "makeCopy" : false});
        }
    });
